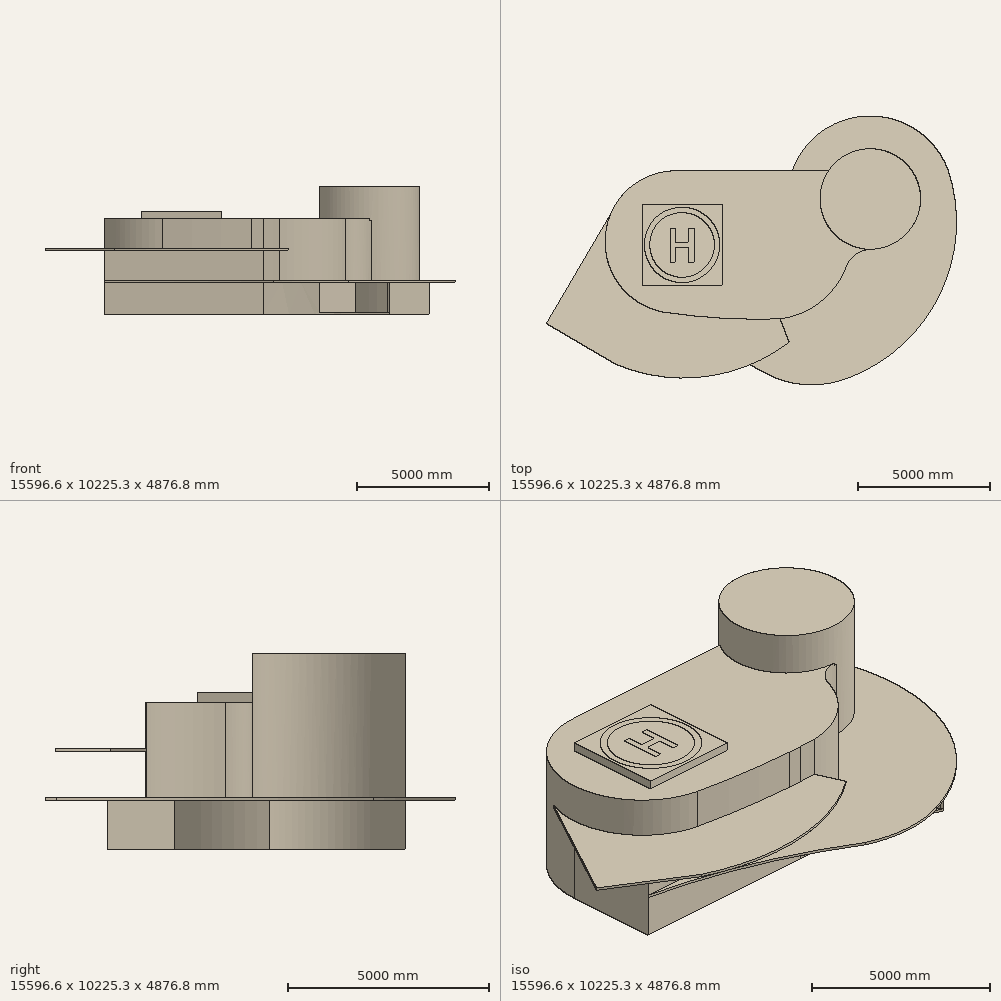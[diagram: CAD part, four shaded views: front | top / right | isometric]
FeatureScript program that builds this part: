
annotation { "Feature Type Name" : "Feature", "Feature Type Description" : "" }
export const myFeature = defineFeature(function(context is Context, id is Id, definition is map)
    precondition{}
    {
        {
            var Q0;
            Q0=qCreatedBy(makeId("Top.planeOp"),FACE);
            var sketch = newSketch(context, id + "F0", { "sketchPlane" : qUnion([Q0])});
            skLineSegment(sketch, "E0.bottom", {"start": v(-2931.38, 2824.35) * mm, "end": v(2865.94, 2824.35) * mm});
            skLineSegment(sketch, "E0.top", {"start": v(-5642.87, -2822.15) * mm, "end": v(428.55, -2822.15) * mm});
            skLineSegment(sketch, "E0.left", {"start": v(-5642.87, 112.86) * mm, "end": v(-5642.87, -2822.15) * mm});
            skPoint(sketch, "E0.middle", {"position": v(0, 0) * mm});
            skArc(sketch, "E1.filletArc", {"start": v(-5638.24, 2823.4) * mm, "mid": v(-5641.62, 2820.24) * mm, "end": v(-5642.87, 2815.8) * mm});
            skArc(sketch, "E2.filletArc", {"start": v(-2931.38, 2824.35) * mm, "mid": v(-4848.7, 2030.17) * mm, "end": v(-5642.87, 112.86) * mm});
            skCircle(sketch, "E3", {"center": v(4446.48, 1748.38) * mm, "radius": 1912.02 * mm});
            skArc(sketch, "E4", {"start": v(5642.42, 256.56) * mm, "mid": v(5941.73, -1032.94) * mm, "end": v(6720.54, -2103.38) * mm});
            skLineSegment(sketch, "E5", {"start": v(5195.79, -3767.67) * mm, "end": v(6720.54, -2103.38) * mm});
            skPoint(sketch, "E6.orphan", {"position": v(5641.46, -2822.15) * mm});
            skArc(sketch, "E7.0", {"start": v(3387.3, 156.55) * mm, "mid": v(3896.4, -1987.67) * mm, "end": v(5195.79, -3767.67) * mm});
            skArc(sketch, "E8", {"start": v(5195.79, -3767.67) * mm, "mid": v(2870.69, -2999.86) * mm, "end": v(428.55, -2822.15) * mm});
            skLineSegment(sketch, "E9", {"start": v(3896.4, -1987.67) * mm, "end": v(2527.33, -2937.98) * mm});
            skArc(sketch, "E10", {"start": v(-1863.52, 1958.6) * mm, "mid": v(-1592.05, 1288.29) * mm, "end": v(-913.5, 1038.14) * mm});
            skLineSegment(sketch, "E11", {"start": v(-1026.45, 1038.14) * mm, "end": v(2671.28, 1038.14) * mm});
            skLineSegment(sketch, "E12", {"start": v(-1863.52, 1958.6) * mm, "end": v(-1836.15, 2824.35) * mm});
            skPoint(sketch, "E12.startSnap0", {"position": v(-1863.52, 1902.1) * mm});
            skSolve(sketch);
        }
        {
            var Q0;
            {var subQ0=sQuery(id+"F0.wireOp",EDGE,"E3");var subQ1=makeQuery(id+"F0.imprint","INTERSECT",VERTEX,{"derivedFrom":[sQuery(id+"F0.wireOp",EDGE,"E0.bottom"),subQ0]});Q0=makeQuery(id+"F0.imprint","IMPRINT",FACE,{"disambiguationData":[TD([[makeQuery(id+"F0.imprint","IMPRINT",EDGE,{"disambiguationData":[TD([[subQ1,-1.0]])],"derivedFrom":subQ0}),1.0]])]});}
            var sketch = newSketch(context, id + "F1", { "sketchPlane" : qUnion([Q0])});
            skArc(sketch, "E13.0.0", {"start": v(2865.94, 2824.35) * mm, "mid": v(2545.72, 1955.54) * mm, "end": v(2671.28, 1038.14) * mm});
            skArc(sketch, "E13.0.1", {"start": v(2671.28, 1038.14) * mm, "mid": v(2962.32, 542.95) * mm, "end": v(3387.3, 156.55) * mm});
            skArc(sketch, "E13.0.2", {"start": v(3387.3, 156.55) * mm, "mid": v(4531.2, -161.75) * mm, "end": v(5642.42, 256.56) * mm});
            skArc(sketch, "E13.0.3", {"start": v(5642.42, 256.56) * mm, "mid": v(5744.7, 3152.1) * mm, "end": v(2865.94, 2824.35) * mm});
            skSolve(sketch);
        }
        {
            var Q0;
            {var subQ8=sQuery(id+"F0.wireOp",EDGE,"E12");Q0=makeQuery(id+"F0.imprint","IMPRINT",FACE,{"disambiguationData":[TD([[makeQuery(id+"F0.imprint","IMPRINT",EDGE,{"derivedFrom":subQ8}),-1.0]])]});}
            var sketch = newSketch(context, id + "F2", { "sketchPlane" : qUnion([Q0])});
            skLineSegment(sketch, "E14.0.0", {"start": v(-1836.15, 2824.35) * mm, "end": v(-1863.52, 1958.6) * mm});
            skArc(sketch, "E14.0.1", {"start": v(-1863.52, 1958.6) * mm, "mid": v(-1631.37, 1328.87) * mm, "end": v(-1026.45, 1038.14) * mm});
            skLineSegment(sketch, "E14.0.2", {"start": v(-1026.45, 1038.14) * mm, "end": v(-913.5, 1038.14) * mm});
            skLineSegment(sketch, "E14.0.3", {"start": v(-913.5, 1038.14) * mm, "end": v(2671.28, 1038.14) * mm});
            skArc(sketch, "E14.0.4", {"start": v(2671.28, 1038.14) * mm, "mid": v(2545.72, 1955.54) * mm, "end": v(2865.94, 2824.35) * mm});
            skLineSegment(sketch, "E14.0.5", {"start": v(2865.94, 2824.35) * mm, "end": v(-1836.15, 2824.35) * mm});
            skSolve(sketch);
        }
        {
            var Q0;
            {var subQ5=sQuery(id+"F0.wireOp",EDGE,"E4");Q0=makeQuery(id+"F0.imprint","IMPRINT",FACE,{"disambiguationData":[TD([[makeQuery(id+"F0.imprint","IMPRINT",EDGE,{"derivedFrom":subQ5}),-1.0]])]});}
            var sketch = newSketch(context, id + "F3", { "sketchPlane" : qUnion([Q0])});
            skArc(sketch, "E15.0.0", {"start": v(5642.42, 256.56) * mm, "mid": v(4531.2, -161.75) * mm, "end": v(3387.3, 156.55) * mm});
            skArc(sketch, "E15.0.1", {"start": v(3387.3, 156.55) * mm, "mid": v(3534.96, -940.94) * mm, "end": v(3896.4, -1987.67) * mm});
            skArc(sketch, "E15.0.2", {"start": v(3896.4, -1987.67) * mm, "mid": v(4457.36, -2942.44) * mm, "end": v(5195.79, -3767.67) * mm});
            skLineSegment(sketch, "E15.0.3", {"start": v(5195.79, -3767.67) * mm, "end": v(6720.54, -2103.38) * mm});
            skArc(sketch, "E15.0.4", {"start": v(6720.54, -2103.38) * mm, "mid": v(5941.73, -1032.94) * mm, "end": v(5642.42, 256.56) * mm});
            skSolve(sketch);
        }
        {
            var Q0;
            {var subQ12=sQuery(id+"F0.wireOp",EDGE,"E0.top");Q0=makeQuery(id+"F0.imprint","IMPRINT",FACE,{"disambiguationData":[TD([[makeQuery(id+"F0.imprint","IMPRINT",EDGE,{"derivedFrom":subQ12}),1.0]])]});}
            var sketch = newSketch(context, id + "F4", { "sketchPlane" : qUnion([Q0])});
            skArc(sketch, "E16.0.0", {"start": v(3387.3, 156.55) * mm, "mid": v(2962.32, 542.95) * mm, "end": v(2671.28, 1038.14) * mm});
            skLineSegment(sketch, "E16.0.1", {"start": v(2671.28, 1038.14) * mm, "end": v(-913.5, 1038.14) * mm});
            skArc(sketch, "E16.0.2", {"start": v(-913.5, 1038.14) * mm, "mid": v(-969.97, 1036.35) * mm, "end": v(-1026.45, 1038.14) * mm});
            skArc(sketch, "E16.0.3", {"start": v(-1026.45, 1038.14) * mm, "mid": v(-1631.37, 1328.87) * mm, "end": v(-1863.52, 1958.6) * mm});
            skLineSegment(sketch, "E16.0.4", {"start": v(-1863.52, 1958.6) * mm, "end": v(-1836.15, 2824.35) * mm});
            skLineSegment(sketch, "E16.0.5", {"start": v(-1836.15, 2824.35) * mm, "end": v(-2931.38, 2824.35) * mm});
            skArc(sketch, "E16.0.6", {"start": v(-2931.38, 2824.35) * mm, "mid": v(-4848.7, 2030.17) * mm, "end": v(-5642.87, 112.86) * mm});
            skLineSegment(sketch, "E16.0.7", {"start": v(-5642.87, 112.86) * mm, "end": v(-5642.87, -2822.15) * mm});
            skLineSegment(sketch, "E16.0.8", {"start": v(-5642.87, -2822.15) * mm, "end": v(428.55, -2822.15) * mm});
            skArc(sketch, "E16.0.9", {"start": v(428.55, -2822.15) * mm, "mid": v(1481, -2824.58) * mm, "end": v(2527.33, -2937.98) * mm});
            skLineSegment(sketch, "E16.0.10", {"start": v(2527.33, -2937.98) * mm, "end": v(3896.4, -1987.67) * mm});
            skArc(sketch, "E16.0.11", {"start": v(3896.4, -1987.67) * mm, "mid": v(3534.96, -940.94) * mm, "end": v(3387.3, 156.55) * mm});
            skLineSegment(sketch, "E17.0.0", {"start": v(-1836.15, 2824.35) * mm, "end": v(-1863.52, 1958.6) * mm});
            skArc(sketch, "E17.0.1", {"start": v(-1863.52, 1958.6) * mm, "mid": v(-1631.37, 1328.87) * mm, "end": v(-1026.45, 1038.14) * mm});
            skLineSegment(sketch, "E17.0.2", {"start": v(-1026.45, 1038.14) * mm, "end": v(-913.5, 1038.14) * mm});
            skLineSegment(sketch, "E17.0.3", {"start": v(-913.5, 1038.14) * mm, "end": v(2671.28, 1038.14) * mm});
            skArc(sketch, "E17.0.4", {"start": v(2671.28, 1038.14) * mm, "mid": v(2545.72, 1955.54) * mm, "end": v(2865.94, 2824.35) * mm});
            skLineSegment(sketch, "E17.0.5", {"start": v(2865.94, 2824.35) * mm, "end": v(-1836.15, 2824.35) * mm});
            skArc(sketch, "E18.0.0", {"start": v(2865.94, 2824.35) * mm, "mid": v(2545.72, 1955.54) * mm, "end": v(2671.28, 1038.14) * mm});
            skArc(sketch, "E18.0.1", {"start": v(2671.28, 1038.14) * mm, "mid": v(2962.32, 542.95) * mm, "end": v(3387.3, 156.55) * mm});
            skArc(sketch, "E18.0.2", {"start": v(3387.3, 156.55) * mm, "mid": v(4531.2, -161.75) * mm, "end": v(5642.42, 256.56) * mm});
            skArc(sketch, "E18.0.3", {"start": v(5642.42, 256.56) * mm, "mid": v(5744.7, 3152.1) * mm, "end": v(2865.94, 2824.35) * mm});
            skArc(sketch, "E19.0.0", {"start": v(5642.42, 256.56) * mm, "mid": v(4531.2, -161.75) * mm, "end": v(3387.3, 156.55) * mm});
            skArc(sketch, "E19.0.1", {"start": v(3387.3, 156.55) * mm, "mid": v(3534.96, -940.94) * mm, "end": v(3896.4, -1987.67) * mm});
            skArc(sketch, "E19.0.2", {"start": v(3896.4, -1987.67) * mm, "mid": v(4457.36, -2942.44) * mm, "end": v(5195.79, -3767.67) * mm});
            skLineSegment(sketch, "E19.0.3", {"start": v(5195.79, -3767.67) * mm, "end": v(6720.54, -2103.38) * mm});
            skArc(sketch, "E19.0.4", {"start": v(6720.54, -2103.38) * mm, "mid": v(5941.73, -1032.94) * mm, "end": v(5642.42, 256.56) * mm});
            skArc(sketch, "E20.0.0", {"start": v(5195.79, -3767.67) * mm, "mid": v(4457.36, -2942.44) * mm, "end": v(3896.4, -1987.67) * mm});
            skLineSegment(sketch, "E20.0.1", {"start": v(3896.4, -1987.67) * mm, "end": v(2527.33, -2937.98) * mm});
            skArc(sketch, "E20.0.2", {"start": v(2527.33, -2937.98) * mm, "mid": v(3890.78, -3258.83) * mm, "end": v(5195.79, -3767.67) * mm});
            skSolve(sketch);
        }
        {
            var Q0;
            Q0 = qSketchRegion(id + "F4", true);
            extrude(context, id + "F5", {"entities" : qUnion([Q0]), "depth" : 76.2 * mm, "offsetDistance" : 25.4 * mm});
        }
        {
            var Q0;
            Q0=makeQuery(id+"F5.opExtrude","CAP_FACE",FACE,{"disambiguationData":[OSD([sQuery(id+"F4.wireOp",EDGE,"E16.0.2"),sQuery(id+"F4.wireOp",EDGE,"E16.0.5"),sQuery(id+"F4.wireOp",EDGE,"E16.0.6"),sQuery(id+"F4.wireOp",EDGE,"E16.0.7"),sQuery(id+"F4.wireOp",EDGE,"E16.0.8"),sQuery(id+"F4.wireOp",EDGE,"E16.0.9"),sQuery(id+"F4.wireOp",EDGE,"E17.0.2"),sQuery(id+"F4.wireOp",EDGE,"E17.0.5"),sQuery(id+"F4.wireOp",EDGE,"E18.0.3"),sQuery(id+"F4.wireOp",EDGE,"E19.0.3"),sQuery(id+"F4.wireOp",EDGE,"E19.0.4"),sQuery(id+"F4.wireOp",EDGE,"E20.0.2")])],"isStart":false});
            var sketch = newSketch(context, id + "F6", { "sketchPlane" : qUnion([Q0])});
            skLineSegment(sketch, "E21.0.0", {"start": v(-5642.87, -2822.15) * mm, "end": v(428.55, -2822.15) * mm});
            skArc(sketch, "E21.0.1", {"start": v(428.55, -2822.15) * mm, "mid": v(1481.87, -2824.63) * mm, "end": v(2529.04, -2938.26) * mm});
            skLineSegment(sketch, "E21.0.2", {"start": v(5195.79, -3767.67) * mm, "end": v(6720.54, -2103.38) * mm});
            skArc(sketch, "E21.0.3", {"start": v(6720.54, -2103.38) * mm, "mid": v(5941.73, -1032.94) * mm, "end": v(5642.42, 256.56) * mm});
            skArc(sketch, "E21.0.4", {"start": v(5642.42, 256.56) * mm, "mid": v(5744.7, 3152.1) * mm, "end": v(2865.94, 2824.35) * mm});
            skLineSegment(sketch, "E21.0.5", {"start": v(2865.94, 2824.35) * mm, "end": v(-2931.38, 2824.35) * mm});
            skArc(sketch, "E21.0.6", {"start": v(-2931.38, 2824.35) * mm, "mid": v(-4848.7, 2030.17) * mm, "end": v(-5642.87, 112.86) * mm});
            skLineSegment(sketch, "E21.0.7", {"start": v(-5642.87, 112.86) * mm, "end": v(-5642.87, -2822.15) * mm});
            skArc(sketch, "E22.0", {"start": v(3387.3, 156.55) * mm, "mid": v(3534.96, -940.94) * mm, "end": v(3896.4, -1987.67) * mm});
            skPoint(sketch, "E23.0", {"position": v(2962.32, 542.95) * mm});
            skArc(sketch, "E24.0", {"start": v(2671.28, 1038.14) * mm, "mid": v(2544.13, 1940.34) * mm, "end": v(2848.95, 2798.95) * mm});
            skLineSegment(sketch, "E25.0", {"start": v(-913.5, 1038.14) * mm, "end": v(2671.28, 1038.14) * mm});
            skArc(sketch, "E26.0", {"start": v(-1863.52, 1958.6) * mm, "mid": v(-1631.37, 1328.87) * mm, "end": v(-1026.45, 1038.14) * mm});
            skPoint(sketch, "E27.0", {"position": v(-1849.83, 2391.48) * mm});
            skLineSegment(sketch, "E28.0", {"start": v(-1836.95, 2798.95) * mm, "end": v(-1863.52, 1958.6) * mm});
            skLineSegment(sketch, "E29.0", {"start": v(2559, -2917.43) * mm, "end": v(3896.4, -1987.67) * mm});
            skArc(sketch, "E30.0", {"start": v(3896.4, -1987.67) * mm, "mid": v(4433, -2908.8) * mm, "end": v(5134.96, -3711.12) * mm});
            skPoint(sketch, "E31.0.end.orphan", {"position": v(3387.3, 156.55) * mm});
            skPoint(sketch, "E31.0.start.orphan", {"position": v(5642.42, 256.56) * mm});
            skPoint(sketch, "E32.0.start.orphan", {"position": v(2671.28, 1038.14) * mm});
            skPoint(sketch, "E33.orphan", {"position": v(-1836.15, 2824.35) * mm});
            skArc(sketch, "E34.0", {"start": v(-2931.38, 2798.95) * mm, "mid": v(-4830.73, 2012.21) * mm, "end": v(-5617.47, 112.86) * mm});
            skLineSegment(sketch, "E34.1", {"start": v(2879.44, 2798.95) * mm, "end": v(-2931.38, 2798.95) * mm});
            skLineSegment(sketch, "E35.0", {"start": v(-5617.47, -2796.75) * mm, "end": v(428.55, -2796.75) * mm});
            skLineSegment(sketch, "E35.1", {"start": v(-5617.47, 112.86) * mm, "end": v(-5617.47, -2796.75) * mm});
            skLineSegment(sketch, "E36.0", {"start": v(5189.7, -3736.7) * mm, "end": v(6684.71, -2104.89) * mm});
            skArc(sketch, "E36.1", {"start": v(427.27, -2796.78) * mm, "mid": v(1496.37, -2800) * mm, "end": v(2559, -2917.43) * mm});
            skArc(sketch, "E37.0", {"start": v(5616.7, 268.55) * mm, "mid": v(5727.14, 3133.74) * mm, "end": v(2879.44, 2798.95) * mm});
            skArc(sketch, "E37.1", {"start": v(6703.39, -2122.11) * mm, "mid": v(6703.38, -2122.11) * mm, "end": v(6703.38, -2122.1) * mm});
            skPoint(sketch, "E38.orphan", {"position": v(2865.94, 2824.35) * mm});
            skPoint(sketch, "E39.orphan", {"position": v(2528.02, -2938.97) * mm});
            skPoint(sketch, "E40.orphan", {"position": v(2559, -2917.43) * mm});
            skPoint(sketch, "E41.orphan", {"position": v(5195.79, -3767.67) * mm});
            skArc(sketch, "E42.trimOffspring", {"start": v(6684.71, -2104.89) * mm, "mid": v(5910.76, -1026.14) * mm, "end": v(5616.7, 268.55) * mm});
            skLineSegment(sketch, "E43", {"start": v(2559, -2917.43) * mm, "end": v(2528.02, -2938.97) * mm});
            skLineSegment(sketch, "E44", {"start": v(5134.96, -3711.12) * mm, "end": v(5195.79, -3767.67) * mm});
            skArc(sketch, "E45.trimOffspring", {"start": v(5134.96, -3711.12) * mm, "mid": v(5162.35, -3723.87) * mm, "end": v(5189.7, -3736.7) * mm});
            skSolve(sketch);
        }
        {
            var Q0;
            Q0=makeQuery(id+"F6.imprint","IMPRINT",FACE,{"disambiguationData":[TD([[makeQuery(id+"F6.imprint","IMPRINT",EDGE,{"derivedFrom":sQuery(id+"F6.wireOp",EDGE,"E21.0.0")}),1.0]])]});
            extrude(context, id + "F7", {"entities" : qUnion([Q0]), "operationType" : NewBodyOperationType.ADD, "depth" : 1143 * mm, "offsetDistance" : 25.4 * mm});
        }
        {
            var Q0;
            Q0=makeQuery(id+"F5.opExtrude","CAP_FACE",FACE,{"disambiguationData":[OSD([sQuery(id+"F4.wireOp",EDGE,"E16.0.2"),sQuery(id+"F4.wireOp",EDGE,"E16.0.5"),sQuery(id+"F4.wireOp",EDGE,"E16.0.6"),sQuery(id+"F4.wireOp",EDGE,"E16.0.7"),sQuery(id+"F4.wireOp",EDGE,"E16.0.8"),sQuery(id+"F4.wireOp",EDGE,"E16.0.9"),sQuery(id+"F4.wireOp",EDGE,"E17.0.2"),sQuery(id+"F4.wireOp",EDGE,"E17.0.5"),sQuery(id+"F4.wireOp",EDGE,"E18.0.3"),sQuery(id+"F4.wireOp",EDGE,"E19.0.3"),sQuery(id+"F4.wireOp",EDGE,"E19.0.4"),sQuery(id+"F4.wireOp",EDGE,"E20.0.2")])],"isStart":false});
            var sketch = newSketch(context, id + "F8", { "sketchPlane" : qUnion([Q0])});
            skLineSegment(sketch, "E46.0", {"start": v(-1836.15, 2824.35) * mm, "end": v(-1863.52, 1958.6) * mm});
            skPoint(sketch, "E47.0", {"position": v(-1631.37, 1328.87) * mm});
            skArc(sketch, "E48.0", {"start": v(-1863.52, 1958.6) * mm, "mid": v(-1631.37, 1328.87) * mm, "end": v(-1026.45, 1038.14) * mm});
            skLineSegment(sketch, "E49.0", {"start": v(-913.5, 1038.14) * mm, "end": v(2671.28, 1038.14) * mm});
            skArc(sketch, "E50.0", {"start": v(2671.28, 1038.14) * mm, "mid": v(2962.32, 542.95) * mm, "end": v(3387.3, 156.55) * mm});
            skArc(sketch, "E51.0", {"start": v(2661.32, 1063.54) * mm, "mid": v(2547.25, 1969.1) * mm, "end": v(2865.94, 2824.35) * mm});
            skArc(sketch, "E52.0", {"start": v(3413.33, 139.53) * mm, "mid": v(4546.73, -161) * mm, "end": v(5642.42, 256.56) * mm});
            skArc(sketch, "E53.0", {"start": v(3387.3, 156.55) * mm, "mid": v(3534.96, -940.94) * mm, "end": v(3896.4, -1987.67) * mm});
            skArc(sketch, "E54.0", {"start": v(3907.24, -2011.06) * mm, "mid": v(4464.98, -2952.84) * mm, "end": v(5195.79, -3767.67) * mm});
            skLineSegment(sketch, "E55.0", {"start": v(3896.4, -1987.67) * mm, "end": v(2527.33, -2937.98) * mm});
            skLineSegment(sketch, "E56.0", {"start": v(-913.5, 1063.54) * mm, "end": v(2671.28, 1063.54) * mm});
            skLineSegment(sketch, "E56.1", {"start": v(-1025.64, 1063.54) * mm, "end": v(-913.5, 1063.54) * mm});
            skArc(sketch, "E56.2", {"start": v(-1838.13, 1957.8) * mm, "mid": v(-1612.85, 1346.26) * mm, "end": v(-1025.64, 1063.54) * mm});
            skLineSegment(sketch, "E56.3", {"start": v(-1810.76, 2823.55) * mm, "end": v(-1838.13, 1957.8) * mm});
            skArc(sketch, "E57.0", {"start": v(2694.86, 1047.58) * mm, "mid": v(2570.97, 1952.78) * mm, "end": v(2886.94, 2810.06) * mm});
            skArc(sketch, "E57.1", {"start": v(2694.86, 1047.58) * mm, "mid": v(2982.04, 558.96) * mm, "end": v(3401.37, 177.7) * mm});
            skArc(sketch, "E57.2", {"start": v(3401.37, 177.7) * mm, "mid": v(4530.07, -136.38) * mm, "end": v(5626.53, 276.38) * mm});
            skArc(sketch, "E58.0", {"start": v(3919.46, -1977.04) * mm, "mid": v(4477.88, -2927.46) * mm, "end": v(5212.94, -3748.94) * mm});
            skArc(sketch, "E58.1", {"start": v(3412.69, 157.42) * mm, "mid": v(3559.68, -935.07) * mm, "end": v(3919.46, -1977.04) * mm});
            skLineSegment(sketch, "E59.0", {"start": v(3910.88, -2008.53) * mm, "end": v(2541.81, -2958.85) * mm});
            skPoint(sketch, "E60.orphan", {"position": v(3896.4, -1987.67) * mm});
            skPoint(sketch, "E61.orphan", {"position": v(3387.3, 156.55) * mm});
            skPoint(sketch, "E62.orphan", {"position": v(2671.28, 1038.14) * mm});
            skLineSegment(sketch, "E63.0", {"start": v(-5617.47, -358.86) * mm, "end": v(-973.35, -358.86) * mm});
            skPoint(sketch, "E64.orphan", {"position": v(-5617.47, 112.86) * mm});
            skPoint(sketch, "E65.0.end.orphan", {"position": v(-5617.47, -2796.75) * mm});
            skArc(sketch, "E66", {"start": v(1489.94, -2799.64) * mm, "mid": v(776.92, -1073.92) * mm, "end": v(-947.95, -358.86) * mm});
            skLineSegment(sketch, "E67.0", {"start": v(-5617.47, -2796.75) * mm, "end": v(427.91, -2796.75) * mm});
            skArc(sketch, "E68.0", {"start": v(427.91, -2796.75) * mm, "mid": v(1496.69, -2800.02) * mm, "end": v(2559, -2917.43) * mm});
            skLineSegment(sketch, "E69", {"start": v(-947.95, -358.86) * mm, "end": v(-947.95, -2796.75) * mm});
            skArc(sketch, "E70.0", {"start": v(1515.34, -2801.09) * mm, "mid": v(795.4, -1056.48) * mm, "end": v(-947.95, -333.46) * mm});
            skLineSegment(sketch, "E70.1", {"start": v(-5617.47, -333.46) * mm, "end": v(-947.95, -333.46) * mm});
            skLineSegment(sketch, "E71.0", {"start": v(-973.35, -358.86) * mm, "end": v(-973.35, -2796.75) * mm});
            skLineSegment(sketch, "E72.0.1", {"start": v(2559, -2917.43) * mm, "end": v(2529.04, -2938.26) * mm});
            skArc(sketch, "E72.0.2", {"start": v(2529.04, -2938.26) * mm, "mid": v(3891.6, -3259.1) * mm, "end": v(5195.79, -3767.67) * mm});
            skLineSegment(sketch, "E72.0.3", {"start": v(5195.79, -3767.67) * mm, "end": v(5134.96, -3711.12) * mm});
            skArc(sketch, "E72.0.4", {"start": v(5134.96, -3711.12) * mm, "mid": v(5162.35, -3723.87) * mm, "end": v(5189.7, -3736.7) * mm});
            skLineSegment(sketch, "E72.0.5", {"start": v(5189.7, -3736.7) * mm, "end": v(6684.71, -2104.89) * mm});
            skArc(sketch, "E72.0.6", {"start": v(6684.71, -2104.89) * mm, "mid": v(5910.76, -1026.14) * mm, "end": v(5616.7, 268.55) * mm});
            skArc(sketch, "E72.0.7", {"start": v(5616.7, 268.55) * mm, "mid": v(5727.14, 3133.74) * mm, "end": v(2879.44, 2798.95) * mm});
            skLineSegment(sketch, "E72.0.8", {"start": v(2879.44, 2798.95) * mm, "end": v(-2931.38, 2798.95) * mm});
            skArc(sketch, "E72.0.9", {"start": v(-2931.38, 2798.95) * mm, "mid": v(-4830.73, 2012.21) * mm, "end": v(-5617.47, 112.86) * mm});
            skLineSegment(sketch, "E72.0.10", {"start": v(-5617.47, 112.86) * mm, "end": v(-5617.47, -2796.75) * mm});
            skArc(sketch, "E73.0.0", {"start": v(2559, -2917.43) * mm, "mid": v(1496.69, -2800.02) * mm, "end": v(427.91, -2796.75) * mm});
            skLineSegment(sketch, "E73.0.1", {"start": v(427.91, -2796.75) * mm, "end": v(-5617.47, -2796.75) * mm});
            skLineSegment(sketch, "E73.0.2", {"start": v(-5617.47, -2796.75) * mm, "end": v(-5617.47, 112.86) * mm});
            skArc(sketch, "E73.0.3", {"start": v(-5617.47, 112.86) * mm, "mid": v(-4830.73, 2012.21) * mm, "end": v(-2931.38, 2798.95) * mm});
            skLineSegment(sketch, "E73.0.4", {"start": v(-2931.38, 2798.95) * mm, "end": v(2879.44, 2798.95) * mm});
            skArc(sketch, "E73.0.5", {"start": v(2879.44, 2798.95) * mm, "mid": v(5727.14, 3133.74) * mm, "end": v(5616.7, 268.55) * mm});
            skArc(sketch, "E73.0.6", {"start": v(5616.7, 268.55) * mm, "mid": v(5910.76, -1026.14) * mm, "end": v(6684.71, -2104.89) * mm});
            skLineSegment(sketch, "E73.0.7", {"start": v(6684.71, -2104.89) * mm, "end": v(5189.7, -3736.7) * mm});
            skArc(sketch, "E73.0.8", {"start": v(5189.7, -3736.7) * mm, "mid": v(5162.35, -3723.87) * mm, "end": v(5134.96, -3711.12) * mm});
            skLineSegment(sketch, "E73.0.9", {"start": v(5134.96, -3711.12) * mm, "end": v(5195.79, -3767.67) * mm});
            skLineSegment(sketch, "E73.0.10", {"start": v(5195.79, -3767.67) * mm, "end": v(6720.54, -2103.38) * mm});
            skArc(sketch, "E73.0.11", {"start": v(6720.54, -2103.38) * mm, "mid": v(5941.73, -1032.94) * mm, "end": v(5642.42, 256.56) * mm});
            skArc(sketch, "E73.0.12", {"start": v(5642.42, 256.56) * mm, "mid": v(5744.7, 3152.1) * mm, "end": v(2865.94, 2824.35) * mm});
            skLineSegment(sketch, "E73.0.13", {"start": v(2865.94, 2824.35) * mm, "end": v(-2931.38, 2824.35) * mm});
            skArc(sketch, "E73.0.14", {"start": v(-2931.38, 2824.35) * mm, "mid": v(-4848.7, 2030.17) * mm, "end": v(-5642.87, 112.86) * mm});
            skLineSegment(sketch, "E73.0.15", {"start": v(-5642.87, 112.86) * mm, "end": v(-5642.87, -2822.15) * mm});
            skLineSegment(sketch, "E73.0.16", {"start": v(-5642.87, -2822.15) * mm, "end": v(428.55, -2822.15) * mm});
            skArc(sketch, "E73.0.17", {"start": v(428.55, -2822.15) * mm, "mid": v(1481.87, -2824.63) * mm, "end": v(2529.04, -2938.26) * mm});
            skLineSegment(sketch, "E73.0.18", {"start": v(2529.04, -2938.26) * mm, "end": v(2559, -2917.43) * mm});
            skLineSegment(sketch, "E74", {"start": v(1489.94, -2799.64) * mm, "end": v(1489.94, -2820.88) * mm});
            skLineSegment(sketch, "E75", {"start": v(1515.34, -2801.09) * mm, "end": v(1515.34, -2819.42) * mm});
            skSolve(sketch);
        }
        {
            var Q0;
            {var subQ23=sQuery(id+"F8.wireOp",EDGE,"E48.0");Q0=makeQuery(id+"F8.imprint","IMPRINT",FACE,{"disambiguationData":[TD([[makeQuery(id+"F8.imprint","IMPRINT",EDGE,{"derivedFrom":subQ23}),1.0]])]});}
            var Q1;
            {var subQ4=sQuery(id+"F8.wireOp",EDGE,"E63.0");Q1=makeQuery(id+"F8.imprint","IMPRINT",FACE,{"disambiguationData":[TD([[makeQuery(id+"F8.imprint","IMPRINT",EDGE,{"derivedFrom":subQ4}),1.0]])]});}
            extrude(context, id + "F9", {"entities" : qUnion([Q0, Q1]), "operationType" : NewBodyOperationType.ADD, "depth" : 1143 * mm, "offsetDistance" : 25.4 * mm});
        }
        {
            var Q0;
            {var subQ0=sQuery(id+"F6.wireOp",EDGE,"E45.trimOffspring");var subQ1=sQuery(id+"F6.wireOp",EDGE,"E43");var subQ2=sQuery(id+"F6.wireOp",EDGE,"E42.trimOffspring");var subQ3=sQuery(id+"F6.wireOp",EDGE,"E36.1");var subQ4=sQuery(id+"F6.wireOp",EDGE,"E36.0");var subQ5=sQuery(id+"F6.wireOp",EDGE,"E34.1");Q0=makeQuery(id+"F9.boolean.opBoolean","MERGE",FACE,{"derivedFrom":[makeQuery(id+"F7.opExtrude","CAP_FACE",FACE,{"disambiguationData":[OSD([sQuery(id+"F6.wireOp",EDGE,"E21.0.0"),sQuery(id+"F6.wireOp",EDGE,"E21.0.1"),sQuery(id+"F6.wireOp",EDGE,"E21.0.2"),sQuery(id+"F6.wireOp",EDGE,"E21.0.3"),sQuery(id+"F6.wireOp",EDGE,"E21.0.4"),sQuery(id+"F6.wireOp",EDGE,"E21.0.5"),sQuery(id+"F6.wireOp",EDGE,"E21.0.6"),sQuery(id+"F6.wireOp",EDGE,"E21.0.7"),sQuery(id+"F6.wireOp",EDGE,"E34.0"),subQ5,sQuery(id+"F6.wireOp",EDGE,"E35.0"),sQuery(id+"F6.wireOp",EDGE,"E35.1"),subQ4,subQ3,sQuery(id+"F6.wireOp",EDGE,"E37.0"),subQ2,subQ1,sQuery(id+"F6.wireOp",EDGE,"E44"),subQ0])],"isStart":false}),makeQuery(id+"F9.opExtrude","CAP_FACE",FACE,{"disambiguationData":[OSD([sQuery(id+"F4.wireOp",EDGE,"E16.0.9"),sQuery(id+"F4.wireOp",EDGE,"E17.0.2"),sQuery(id+"F4.wireOp",EDGE,"E20.0.2"),subQ5,subQ4,subQ3,subQ2,subQ1,subQ0,sQuery(id+"F8.wireOp",EDGE,"E46.0"),sQuery(id+"F8.wireOp",EDGE,"E48.0"),sQuery(id+"F8.wireOp",EDGE,"E49.0"),sQuery(id+"F8.wireOp",EDGE,"E50.0"),sQuery(id+"F8.wireOp",EDGE,"E51.0"),sQuery(id+"F8.wireOp",EDGE,"E52.0"),sQuery(id+"F8.wireOp",EDGE,"E53.0"),sQuery(id+"F8.wireOp",EDGE,"E54.0"),sQuery(id+"F8.wireOp",EDGE,"E55.0"),sQuery(id+"F8.wireOp",EDGE,"E56.0"),sQuery(id+"F8.wireOp",EDGE,"E56.1"),sQuery(id+"F8.wireOp",EDGE,"E56.2"),sQuery(id+"F8.wireOp",EDGE,"E56.3"),sQuery(id+"F8.wireOp",EDGE,"E57.0"),sQuery(id+"F8.wireOp",EDGE,"E57.1"),sQuery(id+"F8.wireOp",EDGE,"E57.2"),sQuery(id+"F8.wireOp",EDGE,"E58.0"),sQuery(id+"F8.wireOp",EDGE,"E58.1"),sQuery(id+"F8.wireOp",EDGE,"E59.0")])],"isStart":false})]});}
            var sketch = newSketch(context, id + "F10", { "sketchPlane" : qUnion([Q0])});
            skArc(sketch, "E76.0", {"start": v(-2931.38, 2824.35) * mm, "mid": v(-4848.7, 2030.17) * mm, "end": v(-5642.87, 112.86) * mm});
            skLineSegment(sketch, "E77.0", {"start": v(-2931.38, 2824.35) * mm, "end": v(2865.94, 2824.35) * mm});
            skArc(sketch, "E78.0", {"start": v(5642.42, 256.56) * mm, "mid": v(5838.4, 437.52) * mm, "end": v(6007.28, 643.98) * mm});
            skLineSegment(sketch, "E79.0", {"start": v(-5642.87, 112.86) * mm, "end": v(-5642.87, -2822.15) * mm});
            skLineSegment(sketch, "E80.0", {"start": v(-5476.28, -2822.15) * mm, "end": v(428.55, -2822.15) * mm});
            skArc(sketch, "E81", {"start": v(4530.95, -161.77) * mm, "mid": v(3930.64, -340.55) * mm, "end": v(3534.96, -826.12) * mm});
            skPoint(sketch, "E81.endSnap0", {"position": v(3534.96, -940.94) * mm});
            skArc(sketch, "E82", {"start": v(1012.9, -2809.76) * mm, "mid": v(2553.73, -2173.7) * mm, "end": v(3534.96, -826.12) * mm});
            skArc(sketch, "E83", {"start": v(3649.58, -5048.57) * mm, "mid": v(5278.85, -3908.21) * mm, "end": v(6162.84, -2126.77) * mm});
            skArc(sketch, "E84", {"start": v(809.14, -5048.57) * mm, "mid": v(-2314.38, -3638.36) * mm, "end": v(-5642.87, -2822.15) * mm});
            skArc(sketch, "E85", {"start": v(809.14, -5048.57) * mm, "mid": v(2229.36, -5320.27) * mm, "end": v(3649.58, -5048.57) * mm});
            skLineSegment(sketch, "E86.0", {"start": v(-5617.47, 112.86) * mm, "end": v(-5617.47, -333.46) * mm});
            skArc(sketch, "E87.0", {"start": v(-2931.38, 2798.95) * mm, "mid": v(-4830.73, 2012.21) * mm, "end": v(-5617.47, 112.86) * mm});
            skLineSegment(sketch, "E88.0", {"start": v(-1836.95, 2798.95) * mm, "end": v(-2931.38, 2798.95) * mm});
            skLineSegment(sketch, "E89.0", {"start": v(2848.95, 2798.95) * mm, "end": v(-1811.54, 2798.95) * mm});
            skLineSegment(sketch, "E90.0", {"start": v(-1811.54, 2798.95) * mm, "end": v(-1838.13, 1957.8) * mm});
            skLineSegment(sketch, "E91.0", {"start": v(-1836.15, 2824.35) * mm, "end": v(-1863.52, 1958.6) * mm});
            skArc(sketch, "E92.0", {"start": v(-1838.13, 1957.8) * mm, "mid": v(-1612.85, 1346.26) * mm, "end": v(-1025.64, 1063.54) * mm});
            skArc(sketch, "E93.0.1", {"start": v(3508.57, -824.23) * mm, "mid": v(3426.19, -336.53) * mm, "end": v(3387.3, 156.55) * mm});
            skArc(sketch, "E93.0.2", {"start": v(3387.3, 156.55) * mm, "mid": v(2962.32, 542.95) * mm, "end": v(2671.28, 1038.14) * mm});
            skLineSegment(sketch, "E93.0.3", {"start": v(2671.28, 1038.14) * mm, "end": v(-913.5, 1038.14) * mm});
            skArc(sketch, "E93.0.4", {"start": v(-913.5, 1038.14) * mm, "mid": v(-969.97, 1036.35) * mm, "end": v(-1026.45, 1038.14) * mm});
            skArc(sketch, "E93.0.5", {"start": v(-1026.45, 1038.14) * mm, "mid": v(-1631.37, 1328.87) * mm, "end": v(-1863.52, 1958.6) * mm});
            skLineSegment(sketch, "E93.0.6", {"start": v(-1863.52, 1958.6) * mm, "end": v(-1863.52, 1958.6) * mm});
            skLineSegment(sketch, "E93.0.9", {"start": v(-5617.47, 112.86) * mm, "end": v(-5617.47, -2796.75) * mm});
            skLineSegment(sketch, "E93.0.10", {"start": v(-5617.47, -2796.75) * mm, "end": v(427.91, -2796.75) * mm});
            skArc(sketch, "E93.0.11", {"start": v(427.91, -2796.75) * mm, "mid": v(719.62, -2786.29) * mm, "end": v(1011.5, -2784.35) * mm});
            skLineSegment(sketch, "E94.0.3", {"start": v(-1025.64, 1063.54) * mm, "end": v(2661.32, 1063.54) * mm});
            skArc(sketch, "E94.0.4", {"start": v(2661.32, 1063.54) * mm, "mid": v(2545.54, 1953.9) * mm, "end": v(2848.95, 2798.95) * mm});
            skCircle(sketch, "E95.0.0", {"center": v(4446.48, 1748.38) * mm, "radius": 1886.62 * mm});
            skArc(sketch, "E96.0", {"start": v(5642.42, 256.56) * mm, "mid": v(5085.63, -53.64) * mm, "end": v(4457.8, -163.6) * mm});
            skArc(sketch, "E97.0", {"start": v(3387.3, 156.55) * mm, "mid": v(3419.74, -282.16) * mm, "end": v(3486.62, -716.95) * mm});
            skArc(sketch, "E98", {"start": v(3520.28, -795.37) * mm, "mid": v(3489.79, -314.38) * mm, "end": v(3387.3, 156.55) * mm});
            skPoint(sketch, "E99.orphan", {"position": v(3413.33, 139.53) * mm});
            skPoint(sketch, "E97.1.end.orphan", {"position": v(5194.26, -3731.74) * mm});
            skPoint(sketch, "E100.orphan", {"position": v(3896.4, -1987.67) * mm});
            skArc(sketch, "E101.0", {"start": v(1011.5, -2784.35) * mm, "mid": v(2538.8, -2153.12) * mm, "end": v(3511.28, -816.94) * mm});
            skArc(sketch, "E101.1", {"start": v(4531.18, -136.37) * mm, "mid": v(4530.84, -136.36) * mm, "end": v(4530.5, -136.36) * mm});
            skArc(sketch, "E102.0", {"start": v(820.14, -5025.61) * mm, "mid": v(-2229.1, -3641.1) * mm, "end": v(-5476.28, -2822.15) * mm});
            skArc(sketch, "E102.1", {"start": v(820.14, -5025.61) * mm, "mid": v(2230.23, -5294.87) * mm, "end": v(3640.2, -5024.97) * mm});
            skArc(sketch, "E103.0", {"start": v(3627.26, -5029.82) * mm, "mid": v(5240.98, -3913.13) * mm, "end": v(6128.87, -2163.05) * mm});
            skArc(sketch, "E104", {"start": v(6162.84, -2126.77) * mm, "mid": v(6174.77, -1694.17) * mm, "end": v(6064.83, -1275.6) * mm});
            skArc(sketch, "E105", {"start": v(6064.83, 731.76) * mm, "mid": v(5885.6, -271.92) * mm, "end": v(6064.83, -1275.6) * mm});
            skArc(sketch, "E106.0", {"start": v(6041, 740.55) * mm, "mid": v(6040.76, 739.9) * mm, "end": v(6040.52, 739.25) * mm});
            skArc(sketch, "E106.1", {"start": v(6137.8, -2122.48) * mm, "mid": v(6149.5, -1696.79) * mm, "end": v(6041.2, -1284.94) * mm});
            skArc(sketch, "E107.trimOffspring", {"start": v(3520.28, -795.37) * mm, "mid": v(3515.72, -806.13) * mm, "end": v(3511.28, -816.94) * mm});
            skArc(sketch, "E108.trimOffspring", {"start": v(3545.87, -740.15) * mm, "mid": v(3513.13, -298.1) * mm, "end": v(3420.01, 135.26) * mm});
            skPoint(sketch, "E109.trimOffspring.end.orphan", {"position": v(3387.3, 156.55) * mm});
            skArc(sketch, "E110.trimOffspring", {"start": v(4303.42, -158.27) * mm, "mid": v(3839.82, -64.84) * mm, "end": v(3413.33, 139.53) * mm});
            skArc(sketch, "E111.trimOffspring", {"start": v(4303.42, -158.27) * mm, "mid": v(3857.47, -361.74) * mm, "end": v(3545.87, -740.15) * mm});
            skArc(sketch, "E112.trimOffspring", {"start": v(6007.28, 643.98) * mm, "mid": v(5860.66, -323.35) * mm, "end": v(6041.2, -1284.94) * mm});
            skArc(sketch, "E113.trimOffspring", {"start": v(6063.43, 727.95) * mm, "mid": v(5494.84, 3347.37) * mm, "end": v(2865.94, 2824.35) * mm});
            skLineSegment(sketch, "E114", {"start": v(6137.8, -2122.48) * mm, "end": v(6128.87, -2163.05) * mm});
            skPoint(sketch, "E115.orphan", {"position": v(-5642.87, -2822.15) * mm});
            skArc(sketch, "E116.0", {"start": v(428.55, -2822.15) * mm, "mid": v(720.63, -2811.67) * mm, "end": v(1012.9, -2809.76) * mm});
            skPoint(sketch, "E117.orphan", {"position": v(2527.33, -2937.98) * mm});
            skSolve(sketch);
        }
        {
            var Q0;
            {var subQ3=sQuery(id+"F10.wireOp",EDGE,"E80.0");Q0=makeQuery(id+"F10.imprint","IMPRINT",FACE,{"disambiguationData":[TD([[makeQuery(id+"F10.imprint","IMPRINT",EDGE,{"derivedFrom":subQ3}),-1.0]])]});}
            var sketch = newSketch(context, id + "F11", { "sketchPlane" : qUnion([Q0])});
            skArc(sketch, "E118.0", {"start": v(809.14, -5048.57) * mm, "mid": v(-2314.38, -3638.36) * mm, "end": v(-5642.87, -2822.15) * mm});
            skLineSegment(sketch, "E119.0", {"start": v(-5642.87, 112.86) * mm, "end": v(-5642.87, -2822.15) * mm});
            skArc(sketch, "E120.0", {"start": v(-2931.38, 2824.35) * mm, "mid": v(-4848.7, 2030.17) * mm, "end": v(-5642.87, 112.86) * mm});
            skLineSegment(sketch, "E121.0", {"start": v(-1836.15, 2824.35) * mm, "end": v(-2931.38, 2824.35) * mm});
            skLineSegment(sketch, "E122.0", {"start": v(2865.94, 2824.35) * mm, "end": v(-1836.15, 2824.35) * mm});
            skArc(sketch, "E123.0", {"start": v(6063.43, 727.95) * mm, "mid": v(5494.84, 3347.37) * mm, "end": v(2865.94, 2824.35) * mm});
            skArc(sketch, "E124.0", {"start": v(809.14, -5048.57) * mm, "mid": v(2229.36, -5320.27) * mm, "end": v(3649.58, -5048.57) * mm});
            skPoint(sketch, "E125.0.end.orphan", {"position": v(5642.42, 256.56) * mm});
            skPoint(sketch, "E125.0.start.orphan", {"position": v(6720.54, -2103.38) * mm});
            skPoint(sketch, "E126.0.start.orphan", {"position": v(5195.79, -3767.67) * mm});
            skArc(sketch, "E127.0", {"start": v(7400.23, 2861.75) * mm, "mid": v(4426.55, 4904.94) * mm, "end": v(1478.9, 2824.35) * mm});
            skArc(sketch, "E128", {"start": v(3649.58, -5048.57) * mm, "mid": v(7115.7, -1847.69) * mm, "end": v(7400.23, 2861.75) * mm});
            skSolve(sketch);
        }
        {
            var Q0;
            Q0 = qSketchRegion(id + "F11", true);
            var Q1;
            {var subQ0=sQuery(id+"F10.wireOp",EDGE,"E104");var subQ1=sQuery(id+"F10.wireOp",EDGE,"E83");var subQ2=makeQuery(id+"F10.imprint","INTERSECT",VERTEX,{"derivedFrom":[subQ1,subQ0]});Q1=makeQuery(id+"F10.imprint","IMPRINT",FACE,{"disambiguationData":[TD([[makeQuery(id+"F10.imprint","IMPRINT",EDGE,{"disambiguationData":[TD([[subQ2,1.0]])],"derivedFrom":subQ1}),-1.0]])]});}
            var Q2;
            {var subQ1=makeQuery(id+"F7.opExtrude","CAP_EDGE",EDGE,{"disambiguationData":[OSD([sQuery(id+"F6.wireOp",EDGE,"E21.0.2")])],"isStart":false});var subQ5=sQuery(id+"F10.wireOp",EDGE,"E83");var subQ6=makeQuery(id+"F10.imprint","INTERSECT",VERTEX,{"derivedFrom":[subQ1,subQ5]});Q2=makeQuery(id+"F10.imprint","IMPRINT",FACE,{"disambiguationData":[TD([[makeQuery(id+"F10.imprint","IMPRINT",EDGE,{"disambiguationData":[TD([[subQ6,-1.0]])],"derivedFrom":subQ5}),-1.0]])]});}
            extrude(context, id + "F12", {"entities" : qUnion([Q0, Q1, Q2]), "operationType" : NewBodyOperationType.ADD, "depth" : 76.2 * mm, "offsetDistance" : 25.4 * mm});
        }
        {
            var Q0;
            Q0=makeQuery(id+"F12.opExtrude","CAP_FACE",FACE,{"disambiguationData":[OSD([sQuery(id+"F11.wireOp",EDGE,"E118.0"),sQuery(id+"F11.wireOp",EDGE,"E119.0"),sQuery(id+"F11.wireOp",EDGE,"E120.0"),sQuery(id+"F11.wireOp",EDGE,"E121.0"),sQuery(id+"F11.wireOp",EDGE,"E122.0"),sQuery(id+"F11.wireOp",EDGE,"E123.0"),sQuery(id+"F11.wireOp",EDGE,"16c1ac02-69e5-49d9-8b1d-dd71bdb8f8db.0"),sQuery(id+"F11.wireOp",EDGE,"cc414059-84ac-49dd-bbb0-032d0c21a76e.0"),sQuery(id+"F11.wireOp",EDGE,"709b0c1b-293d-41bb-91bb-d4a7ccce0465.0"),sQuery(id+"F11.wireOp",EDGE,"E124.0")])],"isStart":false});
            var sketch = newSketch(context, id + "F13", { "sketchPlane" : qUnion([Q0])});
            skLineSegment(sketch, "E129.0", {"start": v(-5642.87, -2822.15) * mm, "end": v(428.55, -2822.15) * mm});
            skArc(sketch, "E130.0", {"start": v(1012.9, -2809.76) * mm, "mid": v(2553.73, -2173.7) * mm, "end": v(3534.96, -826.12) * mm});
            skArc(sketch, "E131.0", {"start": v(1012.9, -2809.76) * mm, "mid": v(720.63, -2811.67) * mm, "end": v(428.55, -2822.15) * mm});
            skPoint(sketch, "E132.orphan", {"position": v(5195.79, -3767.67) * mm});
            skArc(sketch, "E133.0", {"start": v(1011.5, -2784.35) * mm, "mid": v(2538.8, -2153.12) * mm, "end": v(3511.28, -816.94) * mm});
            skArc(sketch, "E134.0", {"start": v(427.91, -2796.75) * mm, "mid": v(719.62, -2786.29) * mm, "end": v(1011.5, -2784.35) * mm});
            skLineSegment(sketch, "E135.0", {"start": v(-5617.47, -2796.75) * mm, "end": v(427.91, -2796.75) * mm});
            skArc(sketch, "E136.0", {"start": v(4303.42, -158.27) * mm, "mid": v(5012.3, -78) * mm, "end": v(5642.42, 256.56) * mm});
            skArc(sketch, "E137.0", {"start": v(4530.95, -161.77) * mm, "mid": v(6116.45, 2679.52) * mm, "end": v(2865.94, 2824.35) * mm});
            skLineSegment(sketch, "E138.0", {"start": v(2865.94, 2824.35) * mm, "end": v(-1836.15, 2824.35) * mm});
            skLineSegment(sketch, "E139.0", {"start": v(-1836.95, 2798.95) * mm, "end": v(-2931.38, 2798.95) * mm});
            skLineSegment(sketch, "E140.0", {"start": v(-1836.15, 2824.35) * mm, "end": v(-2931.38, 2824.35) * mm});
            skArc(sketch, "E141.0", {"start": v(-2931.38, 2824.35) * mm, "mid": v(-4848.7, 2030.17) * mm, "end": v(-5642.87, 112.86) * mm});
            skArc(sketch, "E142.0", {"start": v(-2931.38, 2798.95) * mm, "mid": v(-4830.73, 2012.21) * mm, "end": v(-5617.47, 112.86) * mm});
            skLineSegment(sketch, "E143.0", {"start": v(-5617.47, 112.86) * mm, "end": v(-5617.47, -2796.75) * mm});
            skLineSegment(sketch, "E144.0", {"start": v(-5642.87, 112.86) * mm, "end": v(-5642.87, -2822.15) * mm});
            skPoint(sketch, "E145.orphan", {"position": v(3413.33, 139.53) * mm});
            skPoint(sketch, "E146.orphan", {"position": v(3534.96, -826.12) * mm});
            skPoint(sketch, "E147.0.end.orphan", {"position": v(3545.87, -740.15) * mm});
            skArc(sketch, "E148", {"start": v(3511.28, -816.94) * mm, "mid": v(3463.17, -215.74) * mm, "end": v(3180.78, 317.19) * mm});
            skArc(sketch, "E149.0", {"start": v(3536.5, -820) * mm, "mid": v(3502.94, -265.48) * mm, "end": v(3271.86, 239.72) * mm});
            skArc(sketch, "E150.0", {"start": v(5642.42, 256.56) * mm, "mid": v(4531.2, -161.75) * mm, "end": v(3387.3, 156.55) * mm});
            skArc(sketch, "E151.0", {"start": v(3387.3, 156.55) * mm, "mid": v(3328.8, 197.06) * mm, "end": v(3271.86, 239.72) * mm});
            skPoint(sketch, "E152.orphan", {"position": v(2671.28, 1038.14) * mm});
            skPoint(sketch, "E153.orphan", {"position": v(2848.95, 2798.95) * mm});
            skCircle(sketch, "E154.0", {"center": v(4446.48, 1748.38) * mm, "radius": 1886.62 * mm});
            skArc(sketch, "E155.trimOffspring", {"start": v(3204.77, 328.01) * mm, "mid": v(3202.8, 330.4) * mm, "end": v(3200.83, 332.8) * mm});
            skArc(sketch, "E156.0", {"start": v(2671.28, 1038.14) * mm, "mid": v(2885.84, 643.76) * mm, "end": v(3186.45, 310.29) * mm});
            skArc(sketch, "E157.0", {"start": v(2661.32, 1063.54) * mm, "mid": v(2545.54, 1953.9) * mm, "end": v(2848.95, 2798.95) * mm});
            skLineSegment(sketch, "E158.0", {"start": v(2671.28, 1038.14) * mm, "end": v(-913.5, 1038.14) * mm});
            skLineSegment(sketch, "E159.0", {"start": v(-1025.64, 1063.54) * mm, "end": v(2661.32, 1063.54) * mm});
            skArc(sketch, "E160.0", {"start": v(-1026.45, 1038.14) * mm, "mid": v(-1631.37, 1328.87) * mm, "end": v(-1863.52, 1958.6) * mm});
            skArc(sketch, "E161.0", {"start": v(-1838.13, 1957.8) * mm, "mid": v(-1612.85, 1346.26) * mm, "end": v(-1025.64, 1063.54) * mm});
            skLineSegment(sketch, "E162.0", {"start": v(-1811.54, 2798.95) * mm, "end": v(-1838.13, 1957.8) * mm});
            skLineSegment(sketch, "E163.0", {"start": v(-1836.95, 2798.95) * mm, "end": v(-1863.52, 1958.6) * mm});
            skLineSegment(sketch, "E164.0", {"start": v(-1026.45, 1038.14) * mm, "end": v(-913.5, 1038.14) * mm});
            skArc(sketch, "E165.trimOffspring", {"start": v(3271.86, 239.72) * mm, "mid": v(3328.8, 197.06) * mm, "end": v(3387.3, 156.55) * mm});
            skLineSegment(sketch, "E166.trimOffspring", {"start": v(2848.95, 2798.95) * mm, "end": v(-1811.54, 2798.95) * mm});
            skPoint(sketch, "E167.orphan", {"position": v(2865.94, 2824.35) * mm});
            skPoint(sketch, "E168.orphan", {"position": v(-1836.15, 2824.35) * mm});
            skPoint(sketch, "E169.0.start.orphan", {"position": v(4530.95, -161.77) * mm});
            skArc(sketch, "E170.0", {"start": v(4530.95, -161.77) * mm, "mid": v(3930.64, -340.55) * mm, "end": v(3534.96, -826.12) * mm});
            skArc(sketch, "E171.0.0", {"start": v(3649.58, -5048.57) * mm, "mid": v(5278.85, -3908.21) * mm, "end": v(6162.84, -2126.77) * mm});
            skArc(sketch, "E171.0.1", {"start": v(6162.84, -2126.77) * mm, "mid": v(6174.77, -1694.17) * mm, "end": v(6064.83, -1275.6) * mm});
            skArc(sketch, "E171.0.2", {"start": v(6064.83, -1275.6) * mm, "mid": v(5885.6, -273.95) * mm, "end": v(6063.43, 727.95) * mm});
            skArc(sketch, "E171.0.3", {"start": v(6063.43, 727.95) * mm, "mid": v(5494.84, 3347.37) * mm, "end": v(2865.94, 2824.35) * mm});
            skLineSegment(sketch, "E171.0.4", {"start": v(2865.94, 2824.35) * mm, "end": v(-2931.38, 2824.35) * mm});
            skArc(sketch, "E171.0.7", {"start": v(-5642.87, -2822.15) * mm, "mid": v(-2314.38, -3638.36) * mm, "end": v(809.14, -5048.57) * mm});
            skArc(sketch, "E171.0.8", {"start": v(809.14, -5048.57) * mm, "mid": v(2229.36, -5320.27) * mm, "end": v(3649.58, -5048.57) * mm});
            skArc(sketch, "E172.0", {"start": v(4303.42, -158.27) * mm, "mid": v(3857.47, -361.74) * mm, "end": v(3545.87, -740.15) * mm});
            skSolve(sketch);
        }
        {
            var Q0;
            Q0=makeQuery(id+"F13.imprint","IMPRINT",FACE,{"disambiguationData":[TD([[makeQuery(id+"F13.imprint","IMPRINT",EDGE,{"derivedFrom":sQuery(id+"F13.wireOp",EDGE,"E129.0")}),1.0]])]});
            extrude(context, id + "F14", {"entities" : qUnion([Q0]), "operationType" : NewBodyOperationType.ADD, "depth" : 1143 * mm, "offsetDistance" : 25.4 * mm});
        }
        {
            var Q0;
            Q0=makeQuery(id+"F14.boolean.opBoolean","SPLIT",FACE,{"disambiguationData":[TD([makeQuery(id+"F14.opExtrude","SWEPT_FACE",FACE,{"disambiguationData":[OSD([sQuery(id+"F13.wireOp",EDGE,"E157.0")])]})])],"derivedFrom":makeQuery(id+"F12.boolean.opBoolean","MERGE",FACE,{"derivedFrom":[makeQuery(id+"F12.opExtrude","CAP_FACE",FACE,{"disambiguationData":[OSD([sQuery(id+"F6.wireOp",EDGE,"E21.0.2"),sQuery(id+"F6.wireOp",EDGE,"E21.0.3"),sQuery(id+"F10.wireOp",EDGE,"E83"),sQuery(id+"F10.wireOp",EDGE,"E104")])],"isStart":false}),makeQuery(id+"F12.opExtrude","CAP_FACE",FACE,{"disambiguationData":[OSD([sQuery(id+"F11.wireOp",EDGE,"E118.0"),sQuery(id+"F11.wireOp",EDGE,"E119.0"),sQuery(id+"F11.wireOp",EDGE,"E120.0"),sQuery(id+"F11.wireOp",EDGE,"E121.0"),sQuery(id+"F11.wireOp",EDGE,"E122.0"),sQuery(id+"F11.wireOp",EDGE,"E123.0"),sQuery(id+"F11.wireOp",EDGE,"16c1ac02-69e5-49d9-8b1d-dd71bdb8f8db.0"),sQuery(id+"F11.wireOp",EDGE,"cc414059-84ac-49dd-bbb0-032d0c21a76e.0"),sQuery(id+"F11.wireOp",EDGE,"709b0c1b-293d-41bb-91bb-d4a7ccce0465.0"),sQuery(id+"F11.wireOp",EDGE,"E124.0")])],"isStart":false})]})});
            extrude(context, id + "F15", {"entities" : qUnion([Q0]), "operationType" : NewBodyOperationType.REMOVE, "oppositeDirection" : true, "depth" : 228.6 * mm, "offsetDistance" : 25.4 * mm});
        }
        {
            var Q0;
            Q0=makeQuery(id+"F14.opExtrude","CAP_FACE",FACE,{"disambiguationData":[OSD([sQuery(id+"F13.wireOp",EDGE,"E129.0"),sQuery(id+"F13.wireOp",EDGE,"E130.0"),sQuery(id+"F13.wireOp",EDGE,"E131.0"),sQuery(id+"F13.wireOp",EDGE,"E133.0"),sQuery(id+"F13.wireOp",EDGE,"E134.0"),sQuery(id+"F13.wireOp",EDGE,"E135.0"),sQuery(id+"F13.wireOp",EDGE,"E137.0"),sQuery(id+"F13.wireOp",EDGE,"E139.0"),sQuery(id+"F13.wireOp",EDGE,"E142.0"),sQuery(id+"F13.wireOp",EDGE,"E143.0"),sQuery(id+"F13.wireOp",EDGE,"E148"),sQuery(id+"F13.wireOp",EDGE,"E150.0"),sQuery(id+"F13.wireOp",EDGE,"E154.0"),sQuery(id+"F13.wireOp",EDGE,"E156.0"),sQuery(id+"F13.wireOp",EDGE,"E157.0"),sQuery(id+"F13.wireOp",EDGE,"E158.0"),sQuery(id+"F13.wireOp",EDGE,"E159.0"),sQuery(id+"F13.wireOp",EDGE,"E160.0"),sQuery(id+"F13.wireOp",EDGE,"E161.0"),sQuery(id+"F13.wireOp",EDGE,"E162.0"),sQuery(id+"F13.wireOp",EDGE,"E163.0"),sQuery(id+"F13.wireOp",EDGE,"E164.0"),sQuery(id+"F13.wireOp",EDGE,"E166.trimOffspring"),sQuery(id+"F13.wireOp",EDGE,"E170.0"),sQuery(id+"F13.wireOp",EDGE,"E171.0.3"),sQuery(id+"F13.wireOp",EDGE,"E171.0.4"),sQuery(id+"F13.wireOp",EDGE,"E141.0"),sQuery(id+"F13.wireOp",EDGE,"E144.0")])],"isStart":false});
            var sketch = newSketch(context, id + "F16", { "sketchPlane" : qUnion([Q0])});
            skArc(sketch, "E173.0", {"start": v(-2931.38, 2824.35) * mm, "mid": v(-4848.7, 2030.17) * mm, "end": v(-5642.87, 112.86) * mm});
            skLineSegment(sketch, "E174.0", {"start": v(-1836.15, 2824.35) * mm, "end": v(-2931.38, 2824.35) * mm});
            skLineSegment(sketch, "E175.0", {"start": v(2865.94, 2824.35) * mm, "end": v(-1836.15, 2824.35) * mm});
            skArc(sketch, "E176.0", {"start": v(5642.42, 256.56) * mm, "mid": v(5744.7, 3152.1) * mm, "end": v(2865.94, 2824.35) * mm});
            skArc(sketch, "E177.0", {"start": v(4530.95, -161.77) * mm, "mid": v(3930.64, -340.55) * mm, "end": v(3534.96, -826.12) * mm});
            skArc(sketch, "E178.0", {"start": v(1012.9, -2809.76) * mm, "mid": v(2553.73, -2173.7) * mm, "end": v(3534.96, -826.12) * mm});
            skLineSegment(sketch, "E179.0", {"start": v(-5642.87, -2822.15) * mm, "end": v(428.55, -2822.15) * mm});
            skArc(sketch, "E180.0.0", {"start": v(6302.5, 1289.04) * mm, "mid": v(5657.92, 269.12) * mm, "end": v(4530.95, -161.77) * mm});
            skArc(sketch, "E180.0.2", {"start": v(3534.96, -826.12) * mm, "mid": v(2553.73, -2173.7) * mm, "end": v(1012.9, -2809.76) * mm});
            skArc(sketch, "E180.0.3", {"start": v(1012.9, -2809.76) * mm, "mid": v(720.63, -2811.67) * mm, "end": v(428.55, -2822.15) * mm});
            skLineSegment(sketch, "E180.0.4", {"start": v(428.55, -2822.15) * mm, "end": v(-5642.87, -2822.15) * mm});
            skLineSegment(sketch, "E181.0", {"start": v(-5642.87, 112.86) * mm, "end": v(-5642.87, -2822.15) * mm});
            skSolve(sketch);
        }
        {
            var Q0;
            Q0 = qSketchRegion(id + "F16", true);
            extrude(context, id + "F17", {"entities" : qUnion([Q0]), "operationType" : NewBodyOperationType.ADD, "oppositeDirection" : true, "depth" : 76.2 * mm, "offsetDistance" : 25.4 * mm});
        }
        {
            var Q0;
            Q0=makeQuery(id+"F17.boolean.opBoolean","MERGE",FACE,{"derivedFrom":[makeQuery(id+"F14.opExtrude","CAP_FACE",FACE,{"disambiguationData":[OSD([sQuery(id+"F13.wireOp",EDGE,"E129.0"),sQuery(id+"F13.wireOp",EDGE,"E130.0"),sQuery(id+"F13.wireOp",EDGE,"E131.0"),sQuery(id+"F13.wireOp",EDGE,"E133.0"),sQuery(id+"F13.wireOp",EDGE,"E134.0"),sQuery(id+"F13.wireOp",EDGE,"E135.0"),sQuery(id+"F13.wireOp",EDGE,"E137.0"),sQuery(id+"F13.wireOp",EDGE,"E139.0"),sQuery(id+"F13.wireOp",EDGE,"E142.0"),sQuery(id+"F13.wireOp",EDGE,"E143.0"),sQuery(id+"F13.wireOp",EDGE,"E148"),sQuery(id+"F13.wireOp",EDGE,"E150.0"),sQuery(id+"F13.wireOp",EDGE,"E154.0"),sQuery(id+"F13.wireOp",EDGE,"E156.0"),sQuery(id+"F13.wireOp",EDGE,"E157.0"),sQuery(id+"F13.wireOp",EDGE,"E158.0"),sQuery(id+"F13.wireOp",EDGE,"E159.0"),sQuery(id+"F13.wireOp",EDGE,"E160.0"),sQuery(id+"F13.wireOp",EDGE,"E161.0"),sQuery(id+"F13.wireOp",EDGE,"E162.0"),sQuery(id+"F13.wireOp",EDGE,"E163.0"),sQuery(id+"F13.wireOp",EDGE,"E164.0"),sQuery(id+"F13.wireOp",EDGE,"E166.trimOffspring"),sQuery(id+"F13.wireOp",EDGE,"E170.0"),sQuery(id+"F13.wireOp",EDGE,"E171.0.3"),sQuery(id+"F13.wireOp",EDGE,"E171.0.4"),sQuery(id+"F13.wireOp",EDGE,"E141.0"),sQuery(id+"F13.wireOp",EDGE,"E144.0")])],"isStart":false}),makeQuery(id+"F17.opExtrude","CAP_FACE",FACE,{"disambiguationData":[OSD([sQuery(id+"F16.wireOp",EDGE,"E173.0"),sQuery(id+"F16.wireOp",EDGE,"E174.0"),sQuery(id+"F16.wireOp",EDGE,"E175.0"),sQuery(id+"F16.wireOp",EDGE,"E176.0"),sQuery(id+"F16.wireOp",EDGE,"E180.0.0"),sQuery(id+"F16.wireOp",EDGE,"E177.0"),sQuery(id+"F16.wireOp",EDGE,"E180.0.2"),sQuery(id+"F16.wireOp",EDGE,"E180.0.3"),sQuery(id+"F16.wireOp",EDGE,"E180.0.4"),sQuery(id+"F16.wireOp",EDGE,"E181.0")])],"isStart":true})]});
            var sketch = newSketch(context, id + "F18", { "sketchPlane" : qUnion([Q0])});
            skArc(sketch, "E182.0", {"start": v(6063.43, 727.95) * mm, "mid": v(5494.84, 3347.37) * mm, "end": v(2865.94, 2824.35) * mm});
            skArc(sketch, "E183.0", {"start": v(5642.42, 256.56) * mm, "mid": v(5085.63, -53.64) * mm, "end": v(4457.8, -163.6) * mm});
            skArc(sketch, "E184.0", {"start": v(5642.42, 256.56) * mm, "mid": v(5838.4, 437.52) * mm, "end": v(6007.28, 643.98) * mm});
            skArc(sketch, "E185.0", {"start": v(4530.95, -161.77) * mm, "mid": v(6116.45, 2679.52) * mm, "end": v(2865.94, 2824.35) * mm});
            skArc(sketch, "E186", {"start": v(4457.8, -163.6) * mm, "mid": v(6133.95, 2647.4) * mm, "end": v(2865.94, 2824.35) * mm});
            skCircle(sketch, "E187.0", {"center": v(4446.48, 1748.38) * mm, "radius": 1886.62 * mm});
            skArc(sketch, "E188.0", {"start": v(-2931.38, 2824.35) * mm, "mid": v(-4848.7, 2030.17) * mm, "end": v(-5642.87, 112.86) * mm});
            skArc(sketch, "E189", {"start": v(-2931.38, 2824.35) * mm, "mid": v(-5631.92, 356.28) * mm, "end": v(-3416.26, -2554.92) * mm});
            skLineSegment(sketch, "E190.0", {"start": v(-2931.38, 2824.35) * mm, "end": v(2865.94, 2824.35) * mm});
            skArc(sketch, "E191.0", {"start": v(1012.9, -2809.76) * mm, "mid": v(2553.73, -2173.7) * mm, "end": v(3534.96, -826.12) * mm});
            skArc(sketch, "E192.0", {"start": v(4530.95, -161.77) * mm, "mid": v(3930.64, -340.55) * mm, "end": v(3534.96, -826.12) * mm});
            skArc(sketch, "E193.0", {"start": v(428.55, -2822.15) * mm, "mid": v(720.63, -2811.67) * mm, "end": v(1012.9, -2809.76) * mm});
            skLineSegment(sketch, "E194.0", {"start": v(-26.11, -2822.15) * mm, "end": v(428.55, -2822.15) * mm});
            skArc(sketch, "E195", {"start": v(-3416.26, -2554.92) * mm, "mid": v(-1207.46, -2782.7) * mm, "end": v(1012.9, -2809.76) * mm});
            skPoint(sketch, "E196.orphan", {"position": v(-5476.28, -2822.15) * mm});
            skLineSegment(sketch, "E197.0", {"start": v(-2931.38, 2798.95) * mm, "end": v(-1836.95, 2798.95) * mm});
            skArc(sketch, "E197.1", {"start": v(-2931.38, 2798.95) * mm, "mid": v(-5606.6, 354.2) * mm, "end": v(-3412.11, -2529.86) * mm});
            skArc(sketch, "E198.1", {"start": v(1010.99, -2784.41) * mm, "mid": v(2538.6, -2153.29) * mm, "end": v(3511.28, -816.94) * mm});
            skArc(sketch, "E198.2", {"start": v(-3412.51, -2529.8) * mm, "mid": v(-1206.53, -2757.32) * mm, "end": v(1010.99, -2784.41) * mm});
            skArc(sketch, "E199.trimOffspring", {"start": v(4303.42, -158.27) * mm, "mid": v(3824.56, -388.04) * mm, "end": v(3511.28, -816.94) * mm});
            skArc(sketch, "E200.trimOffspring", {"start": v(2848.95, 2798.95) * mm, "mid": v(2545.54, 1953.9) * mm, "end": v(2661.32, 1063.54) * mm});
            skLineSegment(sketch, "E201.0", {"start": v(-1836.95, 2798.95) * mm, "end": v(-1863.52, 1958.6) * mm});
            skLineSegment(sketch, "E202.0", {"start": v(-1811.54, 2798.95) * mm, "end": v(-1838.13, 1957.8) * mm});
            skLineSegment(sketch, "E203.0", {"start": v(-1025.64, 1063.54) * mm, "end": v(2661.32, 1063.54) * mm});
            skArc(sketch, "E204.0", {"start": v(-1838.13, 1957.8) * mm, "mid": v(-1612.85, 1346.26) * mm, "end": v(-1025.64, 1063.54) * mm});
            skArc(sketch, "E205.0", {"start": v(-1026.45, 1038.14) * mm, "mid": v(-1631.37, 1328.87) * mm, "end": v(-1863.52, 1958.6) * mm});
            skLineSegment(sketch, "E206.0", {"start": v(2671.28, 1038.14) * mm, "end": v(-913.5, 1038.14) * mm});
            skPoint(sketch, "E207.0", {"position": v(-969.97, 1036.35) * mm});
            skArc(sketch, "E208.0", {"start": v(-913.5, 1038.14) * mm, "mid": v(-969.97, 1036.35) * mm, "end": v(-1026.45, 1038.14) * mm});
            skArc(sketch, "E209.trimOffspring", {"start": v(2671.28, 1038.14) * mm, "mid": v(3316.09, 206.3) * mm, "end": v(4303.42, -158.27) * mm});
            skPoint(sketch, "E210.orphan", {"position": v(-1836.15, 2824.35) * mm});
            skLineSegment(sketch, "E211.trimOffspring", {"start": v(-1811.54, 2798.95) * mm, "end": v(2848.95, 2798.95) * mm});
            skSolve(sketch);
        }
        {
            var Q0;
            Q0=makeQuery(id+"F18.imprint","IMPRINT",FACE,{"disambiguationData":[TD([[makeQuery(id+"F18.imprint","IMPRINT",EDGE,{"derivedFrom":sQuery(id+"F18.wireOp",EDGE,"E187.0")}),-1.0]])]});
            extrude(context, id + "F19", {"entities" : qUnion([Q0]), "operationType" : NewBodyOperationType.ADD, "depth" : 1143 * mm, "offsetDistance" : 25.4 * mm});
        }
        {
            var Q0;
            Q0=makeQuery(id+"F19.boolean.opBoolean","SPLIT",FACE,{"disambiguationData":[TD([makeQuery(id+"F19.opExtrude","SWEPT_FACE",FACE,{"disambiguationData":[OSD([sQuery(id+"F18.wireOp",EDGE,"E200.trimOffspring")])]})])],"derivedFrom":makeQuery(id+"F17.boolean.opBoolean","MERGE",FACE,{"derivedFrom":[makeQuery(id+"F14.opExtrude","CAP_FACE",FACE,{"disambiguationData":[OSD([sQuery(id+"F13.wireOp",EDGE,"E129.0"),sQuery(id+"F13.wireOp",EDGE,"E130.0"),sQuery(id+"F13.wireOp",EDGE,"E131.0"),sQuery(id+"F13.wireOp",EDGE,"E133.0"),sQuery(id+"F13.wireOp",EDGE,"E134.0"),sQuery(id+"F13.wireOp",EDGE,"E135.0"),sQuery(id+"F13.wireOp",EDGE,"E137.0"),sQuery(id+"F13.wireOp",EDGE,"E139.0"),sQuery(id+"F13.wireOp",EDGE,"E142.0"),sQuery(id+"F13.wireOp",EDGE,"E143.0"),sQuery(id+"F13.wireOp",EDGE,"E148"),sQuery(id+"F13.wireOp",EDGE,"E150.0"),sQuery(id+"F13.wireOp",EDGE,"E154.0"),sQuery(id+"F13.wireOp",EDGE,"E156.0"),sQuery(id+"F13.wireOp",EDGE,"E157.0"),sQuery(id+"F13.wireOp",EDGE,"E158.0"),sQuery(id+"F13.wireOp",EDGE,"E159.0"),sQuery(id+"F13.wireOp",EDGE,"E160.0"),sQuery(id+"F13.wireOp",EDGE,"E161.0"),sQuery(id+"F13.wireOp",EDGE,"E162.0"),sQuery(id+"F13.wireOp",EDGE,"E163.0"),sQuery(id+"F13.wireOp",EDGE,"E164.0"),sQuery(id+"F13.wireOp",EDGE,"E166.trimOffspring"),sQuery(id+"F13.wireOp",EDGE,"E170.0"),sQuery(id+"F13.wireOp",EDGE,"E171.0.3"),sQuery(id+"F13.wireOp",EDGE,"E171.0.4"),sQuery(id+"F13.wireOp",EDGE,"E141.0"),sQuery(id+"F13.wireOp",EDGE,"E144.0")])],"isStart":false}),makeQuery(id+"F17.opExtrude","CAP_FACE",FACE,{"disambiguationData":[OSD([sQuery(id+"F16.wireOp",EDGE,"E173.0"),sQuery(id+"F16.wireOp",EDGE,"E174.0"),sQuery(id+"F16.wireOp",EDGE,"E175.0"),sQuery(id+"F16.wireOp",EDGE,"E176.0"),sQuery(id+"F16.wireOp",EDGE,"E180.0.0"),sQuery(id+"F16.wireOp",EDGE,"E177.0"),sQuery(id+"F16.wireOp",EDGE,"E180.0.2"),sQuery(id+"F16.wireOp",EDGE,"E180.0.3"),sQuery(id+"F16.wireOp",EDGE,"E180.0.4"),sQuery(id+"F16.wireOp",EDGE,"E181.0")])],"isStart":true})]})});
            extrude(context, id + "F20", {"entities" : qUnion([Q0]), "operationType" : NewBodyOperationType.REMOVE, "oppositeDirection" : true, "depth" : 228.6 * mm, "offsetDistance" : 25.4 * mm});
        }
        {
            var Q0;
            {var subQ0=sQuery(id+"F13.wireOp",EDGE,"E129.0");var subQ1=sQuery(id+"F13.wireOp",EDGE,"E144.0");var subQ2=sQuery(id+"F13.wireOp",EDGE,"E141.0");Q0=makeQuery(id+"F19.boolean.opBoolean","SPLIT",FACE,{"disambiguationData":[TD([makeQuery(id+"F5.opExtrude","SWEPT_FACE",FACE,{"disambiguationData":[OSD([sQuery(id+"F4.wireOp",EDGE,"E16.0.6")])]})])],"derivedFrom":makeQuery(id+"F17.boolean.opBoolean","MERGE",FACE,{"derivedFrom":[makeQuery(id+"F14.opExtrude","CAP_FACE",FACE,{"disambiguationData":[OSD([subQ0,sQuery(id+"F13.wireOp",EDGE,"E130.0"),sQuery(id+"F13.wireOp",EDGE,"E131.0"),sQuery(id+"F13.wireOp",EDGE,"E133.0"),sQuery(id+"F13.wireOp",EDGE,"E134.0"),sQuery(id+"F13.wireOp",EDGE,"E135.0"),sQuery(id+"F13.wireOp",EDGE,"E137.0"),sQuery(id+"F13.wireOp",EDGE,"E139.0"),sQuery(id+"F13.wireOp",EDGE,"E142.0"),sQuery(id+"F13.wireOp",EDGE,"E143.0"),sQuery(id+"F13.wireOp",EDGE,"E148"),sQuery(id+"F13.wireOp",EDGE,"E150.0"),sQuery(id+"F13.wireOp",EDGE,"E154.0"),sQuery(id+"F13.wireOp",EDGE,"E156.0"),sQuery(id+"F13.wireOp",EDGE,"E157.0"),sQuery(id+"F13.wireOp",EDGE,"E158.0"),sQuery(id+"F13.wireOp",EDGE,"E159.0"),sQuery(id+"F13.wireOp",EDGE,"E160.0"),sQuery(id+"F13.wireOp",EDGE,"E161.0"),sQuery(id+"F13.wireOp",EDGE,"E162.0"),sQuery(id+"F13.wireOp",EDGE,"E163.0"),sQuery(id+"F13.wireOp",EDGE,"E164.0"),sQuery(id+"F13.wireOp",EDGE,"E166.trimOffspring"),sQuery(id+"F13.wireOp",EDGE,"E170.0"),sQuery(id+"F13.wireOp",EDGE,"E171.0.3"),sQuery(id+"F13.wireOp",EDGE,"E171.0.4"),subQ2,subQ1])],"isStart":false}),makeQuery(id+"F17.opExtrude","CAP_FACE",FACE,{"disambiguationData":[OSD([sQuery(id+"F16.wireOp",EDGE,"E173.0"),sQuery(id+"F16.wireOp",EDGE,"E174.0"),sQuery(id+"F16.wireOp",EDGE,"E175.0"),sQuery(id+"F16.wireOp",EDGE,"E176.0"),sQuery(id+"F16.wireOp",EDGE,"E180.0.0"),sQuery(id+"F16.wireOp",EDGE,"E177.0"),sQuery(id+"F16.wireOp",EDGE,"E180.0.2"),sQuery(id+"F16.wireOp",EDGE,"E180.0.3"),sQuery(id+"F16.wireOp",EDGE,"E180.0.4"),sQuery(id+"F16.wireOp",EDGE,"E181.0")])],"isStart":true})]})});}
            var sketch = newSketch(context, id + "F21", { "sketchPlane" : qUnion([Q0])});
            skArc(sketch, "E212.0", {"start": v(-2931.38, 2824.35) * mm, "mid": v(-4428.47, 2373.59) * mm, "end": v(-5427.8, 1171.17) * mm});
            skLineSegment(sketch, "E213.0", {"start": v(2865.94, 2824.35) * mm, "end": v(-2931.38, 2824.35) * mm});
            skArc(sketch, "E214.0", {"start": v(4530.95, -161.77) * mm, "mid": v(6116.45, 2679.52) * mm, "end": v(2865.94, 2824.35) * mm});
            skArc(sketch, "E215.0", {"start": v(4530.95, -161.77) * mm, "mid": v(3930.64, -340.55) * mm, "end": v(3534.96, -826.12) * mm});
            skArc(sketch, "E216.0", {"start": v(3467.77, -992.6) * mm, "mid": v(3502.58, -909.85) * mm, "end": v(3534.96, -826.12) * mm});
            skArc(sketch, "E217.0.0", {"start": v(6302.5, 1289.04) * mm, "mid": v(5657.92, 269.12) * mm, "end": v(4530.95, -161.77) * mm});
            skArc(sketch, "E217.0.2", {"start": v(3534.96, -826.12) * mm, "mid": v(3502.58, -909.85) * mm, "end": v(3467.77, -992.6) * mm});
            skArc(sketch, "E217.0.3", {"start": v(1012.9, -2809.76) * mm, "mid": v(720.63, -2811.67) * mm, "end": v(428.55, -2822.15) * mm});
            skPoint(sketch, "E217.0.6.start.orphan", {"position": v(809.14, -5048.57) * mm});
            skPoint(sketch, "E217.0.7.start.orphan", {"position": v(3649.58, -5048.57) * mm});
            skPoint(sketch, "E217.0.8.start.orphan", {"position": v(6720.54, -2103.38) * mm});
            skLineSegment(sketch, "E218", {"start": v(-5427.8, 1171.17) * mm, "end": v(-7871.32, -2990.5) * mm});
            skLineSegment(sketch, "E219", {"start": v(-7871.32, -2990.5) * mm, "end": v(-5242.9, -4533.77) * mm});
            skArc(sketch, "E220", {"start": v(-5242.9, -4533.77) * mm, "mid": v(-1829.51, -5010.06) * mm, "end": v(1362.3, -3709.9) * mm});
            skPoint(sketch, "E221.orphan", {"position": v(-3416.26, -2554.92) * mm});
            skPoint(sketch, "E217.0.4.end.orphan", {"position": v(-5642.87, -2822.15) * mm});
            skPoint(sketch, "E222.orphan", {"position": v(1012.9, -2809.76) * mm});
            skLineSegment(sketch, "E223", {"start": v(1012.9, -2809.76) * mm, "end": v(1362.3, -3709.9) * mm});
            skArc(sketch, "E224.trimOffspring", {"start": v(3467.77, -992.6) * mm, "mid": v(3501.93, -909.59) * mm, "end": v(3534.96, -826.12) * mm});
            skArc(sketch, "E225.0", {"start": v(1012.9, -2809.76) * mm, "mid": v(2553.73, -2173.7) * mm, "end": v(3534.96, -826.12) * mm});
            skSolve(sketch);
        }
        {
            var Q0;
            Q0 = qSketchRegion(id + "F21", true);
            extrude(context, id + "F22", {"entities" : qUnion([Q0]), "operationType" : NewBodyOperationType.ADD, "depth" : 76.2 * mm, "offsetDistance" : 25.4 * mm});
        }
        {
            var Q0;
            Q0=makeQuery(id+"F19.opExtrude","CAP_FACE",FACE,{"disambiguationData":[OSD([sQuery(id+"F18.wireOp",EDGE,"E186"),sQuery(id+"F18.wireOp",EDGE,"E187.0"),sQuery(id+"F18.wireOp",EDGE,"E189"),sQuery(id+"F18.wireOp",EDGE,"E190.0"),sQuery(id+"F18.wireOp",EDGE,"E191.0"),sQuery(id+"F18.wireOp",EDGE,"E192.0"),sQuery(id+"F18.wireOp",EDGE,"E193.0"),sQuery(id+"F18.wireOp",EDGE,"E194.0"),sQuery(id+"F18.wireOp",EDGE,"E195"),sQuery(id+"F18.wireOp",EDGE,"E197.0"),sQuery(id+"F18.wireOp",EDGE,"E197.1"),sQuery(id+"F18.wireOp",EDGE,"E198.1"),sQuery(id+"F18.wireOp",EDGE,"E198.2"),sQuery(id+"F18.wireOp",EDGE,"E199.trimOffspring"),sQuery(id+"F18.wireOp",EDGE,"E200.trimOffspring"),sQuery(id+"F18.wireOp",EDGE,"E201.0"),sQuery(id+"F18.wireOp",EDGE,"E202.0"),sQuery(id+"F18.wireOp",EDGE,"E203.0"),sQuery(id+"F18.wireOp",EDGE,"E204.0"),sQuery(id+"F18.wireOp",EDGE,"E205.0"),sQuery(id+"F18.wireOp",EDGE,"E206.0"),sQuery(id+"F18.wireOp",EDGE,"E208.0"),sQuery(id+"F18.wireOp",EDGE,"E209.trimOffspring"),sQuery(id+"F18.wireOp",EDGE,"E211.trimOffspring")])],"isStart":false});
            var sketch = newSketch(context, id + "F23", { "sketchPlane" : qUnion([Q0])});
            skArc(sketch, "E226.0", {"start": v(4530.95, -161.77) * mm, "mid": v(6116.45, 2679.52) * mm, "end": v(2865.94, 2824.35) * mm});
            skArc(sketch, "E227", {"start": v(4457.8, -163.6) * mm, "mid": v(6133.95, 2647.4) * mm, "end": v(2865.94, 2824.35) * mm});
            skArc(sketch, "E228.0", {"start": v(4530.95, -161.77) * mm, "mid": v(3930.64, -340.55) * mm, "end": v(3534.96, -826.12) * mm});
            skArc(sketch, "E229.0", {"start": v(1012.9, -2809.76) * mm, "mid": v(2553.73, -2173.7) * mm, "end": v(3534.96, -826.12) * mm});
            skArc(sketch, "E230.0", {"start": v(1012.9, -2809.76) * mm, "mid": v(720.63, -2811.67) * mm, "end": v(428.55, -2822.15) * mm});
            skLineSegment(sketch, "E231.0", {"start": v(-26.11, -2822.15) * mm, "end": v(428.55, -2822.15) * mm});
            skArc(sketch, "E232.0", {"start": v(-3416.26, -2554.92) * mm, "mid": v(-1725.82, -2747.37) * mm, "end": v(-26.11, -2822.15) * mm});
            skArc(sketch, "E233.0", {"start": v(-2931.38, 2824.35) * mm, "mid": v(-5631.92, 356.28) * mm, "end": v(-3416.26, -2554.92) * mm});
            skLineSegment(sketch, "E234.0", {"start": v(2865.94, 2824.35) * mm, "end": v(-2931.38, 2824.35) * mm});
            skSolve(sketch);
        }
        {
            var Q0;
            Q0 = qSketchRegion(id + "F23", true);
            extrude(context, id + "F24", {"entities" : qUnion([Q0]), "operationType" : NewBodyOperationType.ADD, "depth" : 76.2 * mm, "offsetDistance" : 25.4 * mm});
        }
        {
            var Q0;
            Q0=makeQuery(id+"F24.opExtrude","CAP_FACE",FACE,{"disambiguationData":[OSD([sQuery(id+"F23.wireOp",EDGE,"E227"),sQuery(id+"F23.wireOp",EDGE,"E228.0"),sQuery(id+"F23.wireOp",EDGE,"E229.0"),sQuery(id+"F23.wireOp",EDGE,"E230.0"),sQuery(id+"F23.wireOp",EDGE,"E231.0"),sQuery(id+"F23.wireOp",EDGE,"E232.0"),sQuery(id+"F23.wireOp",EDGE,"E233.0"),sQuery(id+"F23.wireOp",EDGE,"E234.0")])],"isStart":false});
            var sketch = newSketch(context, id + "F25", { "sketchPlane" : qUnion([Q0])});
            skArc(sketch, "E235.0", {"start": v(4457.8, -163.6) * mm, "mid": v(6133.95, 2647.4) * mm, "end": v(2865.94, 2824.35) * mm});
            skCircle(sketch, "E236", {"center": v(4446.48, 1748.38) * mm, "radius": 1912.02 * mm});
            skCircle(sketch, "E237.0", {"center": v(4446.48, 1748.38) * mm, "radius": 1886.62 * mm});
            skSolve(sketch);
        }
        {
            var Q0;
            Q0=makeQuery(id+"F25.imprint","IMPRINT",FACE,{"disambiguationData":[TD([[makeQuery(id+"F25.imprint","IMPRINT",EDGE,{"derivedFrom":sQuery(id+"F25.wireOp",EDGE,"E237.0")}),-1.0]])]});
            extrude(context, id + "F26", {"entities" : qUnion([Q0]), "operationType" : NewBodyOperationType.ADD, "depth" : 1143 * mm, "offsetDistance" : 25.4 * mm});
        }
        {
            var Q0;
            Q0=makeQuery(id+"F26.opExtrude","CAP_FACE",FACE,{"disambiguationData":[OSD([sQuery(id+"F25.wireOp",EDGE,"E236"),sQuery(id+"F25.wireOp",EDGE,"E237.0")])],"isStart":false});
            var sketch = newSketch(context, id + "F27", { "sketchPlane" : qUnion([Q0])});
            skCircle(sketch, "E238.0", {"center": v(4446.48, 1748.38) * mm, "radius": 1912.02 * mm});
            skSolve(sketch);
        }
        {
            var Q0;
            Q0 = qSketchRegion(id + "F27", true);
            extrude(context, id + "F28", {"entities" : qUnion([Q0]), "operationType" : NewBodyOperationType.ADD, "depth" : 76.2 * mm, "offsetDistance" : 25.4 * mm});
        }
        {
            var Q0;
            {var subQ0=sQuery(id+"F23.wireOp",EDGE,"E227");var subQ1=sQuery(id+"F23.wireOp",EDGE,"E228.0");var subQ2=sQuery(id+"F23.wireOp",EDGE,"E229.0");var subQ3=sQuery(id+"F23.wireOp",EDGE,"E230.0");var subQ4=sQuery(id+"F23.wireOp",EDGE,"E231.0");var subQ5=sQuery(id+"F23.wireOp",EDGE,"E232.0");var subQ6=sQuery(id+"F23.wireOp",EDGE,"E233.0");var subQ7=sQuery(id+"F23.wireOp",EDGE,"E234.0");Q0=makeQuery(id+"F26.boolean.opBoolean","SPLIT",FACE,{"disambiguationData":[TD([makeQuery(id+"F5.opExtrude","SWEPT_FACE",FACE,{"disambiguationData":[OSD([sQuery(id+"F4.wireOp",EDGE,"E16.0.6")])]})])],"derivedFrom":makeQuery(id+"F24.opExtrude","CAP_FACE",FACE,{"disambiguationData":[OSD([subQ0,subQ1,subQ2,subQ3,subQ4,subQ5,subQ6,subQ7])],"isStart":false})});}
            var sketch = newSketch(context, id + "F29", { "sketchPlane" : qUnion([Q0])});
            skLineSegment(sketch, "E239.bottom", {"start": v(-1189.47, 1524) * mm, "end": v(-4237.47, 1524) * mm});
            skLineSegment(sketch, "E239.top", {"start": v(-1189.47, -1524) * mm, "end": v(-4237.47, -1524) * mm});
            skLineSegment(sketch, "E239.left", {"start": v(-1189.47, 1524) * mm, "end": v(-1189.47, -1524) * mm});
            skLineSegment(sketch, "E239.right", {"start": v(-4237.47, 1524) * mm, "end": v(-4237.47, -1524) * mm});
            skPoint(sketch, "E239.middle", {"position": v(-2713.47, 0) * mm});
            skCircle(sketch, "E240", {"center": v(-2713.47, 0) * mm, "radius": 1433.38 * mm});
            skCircle(sketch, "E241.0", {"center": v(-2713.47, 0) * mm, "radius": 1230.18 * mm});
            skLineSegment(sketch, "E242.bottom", {"start": v(-2464.8, 101.6) * mm, "end": v(-2962.14, 101.6) * mm});
            skLineSegment(sketch, "E242.top", {"start": v(-2464.8, -101.6) * mm, "end": v(-2962.14, -101.6) * mm});
            skLineSegment(sketch, "E243.bottom", {"start": v(-3165.34, 615.53) * mm, "end": v(-2962.14, 615.53) * mm});
            skLineSegment(sketch, "E243.top", {"start": v(-3165.34, -654.47) * mm, "end": v(-2962.14, -654.47) * mm});
            skLineSegment(sketch, "E243.left", {"start": v(-3165.34, 615.53) * mm, "end": v(-3165.34, -654.47) * mm});
            skLineSegment(sketch, "E243.right", {"start": v(-2962.14, 615.53) * mm, "end": v(-2962.14, 101.6) * mm});
            skLineSegment(sketch, "E244.MirrorCS", {"start": v(-2464.8, 615.53) * mm, "end": v(-2464.8, 101.6) * mm});
            skLineSegment(sketch, "E245.MirrorCS", {"start": v(-2261.6, 615.53) * mm, "end": v(-2464.8, 615.53) * mm});
            skLineSegment(sketch, "E246.MirrorCS", {"start": v(-2261.6, 615.53) * mm, "end": v(-2261.6, -654.47) * mm});
            skLineSegment(sketch, "E247.MirrorCS", {"start": v(-2261.6, -654.47) * mm, "end": v(-2464.8, -654.47) * mm});
            skLineSegment(sketch, "E248.trimOffspring", {"start": v(-2464.8, -101.6) * mm, "end": v(-2464.8, -654.47) * mm});
            skLineSegment(sketch, "E249.trimOffspring", {"start": v(-2962.14, -101.6) * mm, "end": v(-2962.14, -654.47) * mm});
            skSolve(sketch);
        }
        {
            var Q0;
            Q0=makeQuery(id+"F29.imprint","IMPRINT",FACE,{"disambiguationData":[TD([[makeQuery(id+"F29.imprint","IMPRINT",EDGE,{"derivedFrom":sQuery(id+"F29.wireOp",EDGE,"E239.bottom")}),1.0]])]});
            var sketch = newSketch(context, id + "F30", { "sketchPlane" : qUnion([Q0])});
            skCircle(sketch, "E250.0", {"center": v(-2713.47, 0) * mm, "radius": 1433.38 * mm});
            skCircle(sketch, "E251.0", {"center": v(-2713.47, 0) * mm, "radius": 1230.18 * mm});
            skLineSegment(sketch, "E252.0", {"start": v(-2261.6, 615.53) * mm, "end": v(-2261.6, -654.47) * mm});
            skPoint(sketch, "E253.0", {"position": v(-2464.8, 358.57) * mm});
            skPoint(sketch, "E254.0", {"position": v(-2962.14, 358.57) * mm});
            skLineSegment(sketch, "E255.0", {"start": v(-3165.34, 615.53) * mm, "end": v(-3165.34, -654.47) * mm});
            skLineSegment(sketch, "E256.0", {"start": v(-2962.14, 615.53) * mm, "end": v(-2962.14, 101.6) * mm});
            skLineSegment(sketch, "E257.0.1", {"start": v(-3165.34, -654.47) * mm, "end": v(-2962.14, -654.47) * mm});
            skLineSegment(sketch, "E257.0.2", {"start": v(-2962.14, -654.47) * mm, "end": v(-2962.14, -101.6) * mm});
            skLineSegment(sketch, "E257.0.3", {"start": v(-2962.14, -101.6) * mm, "end": v(-2464.8, -101.6) * mm});
            skLineSegment(sketch, "E257.0.4", {"start": v(-2464.8, -101.6) * mm, "end": v(-2464.8, -654.47) * mm});
            skLineSegment(sketch, "E257.0.5", {"start": v(-2464.8, -654.47) * mm, "end": v(-2261.6, -654.47) * mm});
            skLineSegment(sketch, "E257.0.6", {"start": v(-2261.6, -654.47) * mm, "end": v(-2261.6, 615.53) * mm});
            skLineSegment(sketch, "E257.0.7", {"start": v(-2261.6, 615.53) * mm, "end": v(-2464.8, 615.53) * mm});
            skLineSegment(sketch, "E257.0.8", {"start": v(-2464.8, 615.53) * mm, "end": v(-2464.8, 101.6) * mm});
            skLineSegment(sketch, "E257.0.9", {"start": v(-2464.8, 101.6) * mm, "end": v(-2962.14, 101.6) * mm});
            skLineSegment(sketch, "E257.0.10", {"start": v(-2962.14, 101.6) * mm, "end": v(-2962.14, 615.53) * mm});
            skLineSegment(sketch, "E257.0.11", {"start": v(-2962.14, 615.53) * mm, "end": v(-3165.34, 615.53) * mm});
            skSolve(sketch);
        }
        {
            var Q0;
            Q0 = qSketchRegion(id + "F29", true);
            var Q1;
            Q1=makeQuery(id+"F29.imprint","IMPRINT",FACE,{"disambiguationData":[TD([[makeQuery(id+"F29.imprint","IMPRINT",EDGE,{"derivedFrom":sQuery(id+"F29.wireOp",EDGE,"E241.0")}),1.0]])]});
            var Q2;
            Q2=makeQuery(id+"F29.imprint","IMPRINT",FACE,{"disambiguationData":[TD([[makeQuery(id+"F29.imprint","IMPRINT",EDGE,{"derivedFrom":sQuery(id+"F29.wireOp",EDGE,"E242.bottom")}),1.0]])]});
            var Q3;
            Q3=makeQuery(id+"F29.imprint","IMPRINT",FACE,{"disambiguationData":[TD([[makeQuery(id+"F29.imprint","IMPRINT",EDGE,{"derivedFrom":sQuery(id+"F29.wireOp",EDGE,"E240")}),1.0]])]});
            extrude(context, id + "F31", {"entities" : qUnion([Q0, Q1, Q2, Q3]), "operationType" : NewBodyOperationType.ADD, "depth" : 254 * mm, "offsetDistance" : 25.4 * mm});
        }
        {
            var Q0;
            Q0=makeQuery(id+"F31.opExtrude","CAP_FACE",FACE,{"disambiguationData":[OSD([sQuery(id+"F29.wireOp",EDGE,"E239.bottom"),sQuery(id+"F29.wireOp",EDGE,"E239.top"),sQuery(id+"F29.wireOp",EDGE,"E239.left"),sQuery(id+"F29.wireOp",EDGE,"E239.right")])],"isStart":false});
            var sketch = newSketch(context, id + "F32", { "sketchPlane" : qUnion([Q0])});
            skLineSegment(sketch, "E258.0", {"start": v(-3165.34, 615.53) * mm, "end": v(-3165.34, -654.47) * mm});
            skLineSegment(sketch, "E259.0", {"start": v(-2962.14, 615.53) * mm, "end": v(-3165.34, 615.53) * mm});
            skLineSegment(sketch, "E260.0", {"start": v(-2962.14, 615.53) * mm, "end": v(-2962.14, 101.6) * mm});
            skPoint(sketch, "E261.0", {"position": v(-2713.47, 101.6) * mm});
            skLineSegment(sketch, "E262.0", {"start": v(-2464.8, 101.6) * mm, "end": v(-2962.14, 101.6) * mm});
            skLineSegment(sketch, "E263.0", {"start": v(-2464.8, 615.53) * mm, "end": v(-2464.8, 101.6) * mm});
            skPoint(sketch, "E264.0", {"position": v(-2363.2, 615.53) * mm});
            skLineSegment(sketch, "E265.0", {"start": v(-2261.6, 615.53) * mm, "end": v(-2464.8, 615.53) * mm});
            skLineSegment(sketch, "E266.0", {"start": v(-2261.6, -654.47) * mm, "end": v(-2261.6, 615.53) * mm});
            skLineSegment(sketch, "E267.0", {"start": v(-2464.8, -101.6) * mm, "end": v(-2464.8, -654.47) * mm});
            skLineSegment(sketch, "E268.0", {"start": v(-2962.14, -101.6) * mm, "end": v(-2464.8, -101.6) * mm});
            skLineSegment(sketch, "E269.0", {"start": v(-2962.14, -654.47) * mm, "end": v(-2962.14, -101.6) * mm});
            skLineSegment(sketch, "E270.0", {"start": v(-3165.34, -654.47) * mm, "end": v(-2962.14, -654.47) * mm});
            skLineSegment(sketch, "E271.0", {"start": v(-2464.8, -654.47) * mm, "end": v(-2261.6, -654.47) * mm});
            skSolve(sketch);
        }
        {
            var Q0;
            Q0 = qSketchRegion(id + "F32", true);
            extrude(context, id + "F33", {"entities" : qUnion([Q0]), "operationType" : NewBodyOperationType.ADD, "depth" : 0.03 * mm, "offsetDistance" : 25.4 * mm});
        }
        {
            var Q0;
            Q0=makeQuery(id+"F31.opExtrude","CAP_FACE",FACE,{"disambiguationData":[OSD([sQuery(id+"F29.wireOp",EDGE,"E239.bottom"),sQuery(id+"F29.wireOp",EDGE,"E239.top"),sQuery(id+"F29.wireOp",EDGE,"E239.left"),sQuery(id+"F29.wireOp",EDGE,"E239.right")])],"isStart":false});
            var sketch = newSketch(context, id + "F34", { "sketchPlane" : qUnion([Q0])});
            skCircle(sketch, "E272.0", {"center": v(-2713.47, 0) * mm, "radius": 1433.38 * mm});
            skCircle(sketch, "E273.0", {"center": v(-2713.47, 0) * mm, "radius": 1230.18 * mm});
            skSolve(sketch);
        }
        {
            var Q0;
            Q0=makeQuery(id+"F34.imprint","IMPRINT",FACE,{"disambiguationData":[TD([[makeQuery(id+"F34.imprint","IMPRINT",EDGE,{"derivedFrom":sQuery(id+"F34.wireOp",EDGE,"E272.0")}),1.0]])]});
            extrude(context, id + "F35", {"entities" : qUnion([Q0]), "operationType" : NewBodyOperationType.ADD, "depth" : 0.03 * mm, "offsetDistance" : 25.4 * mm});
        }
    });
